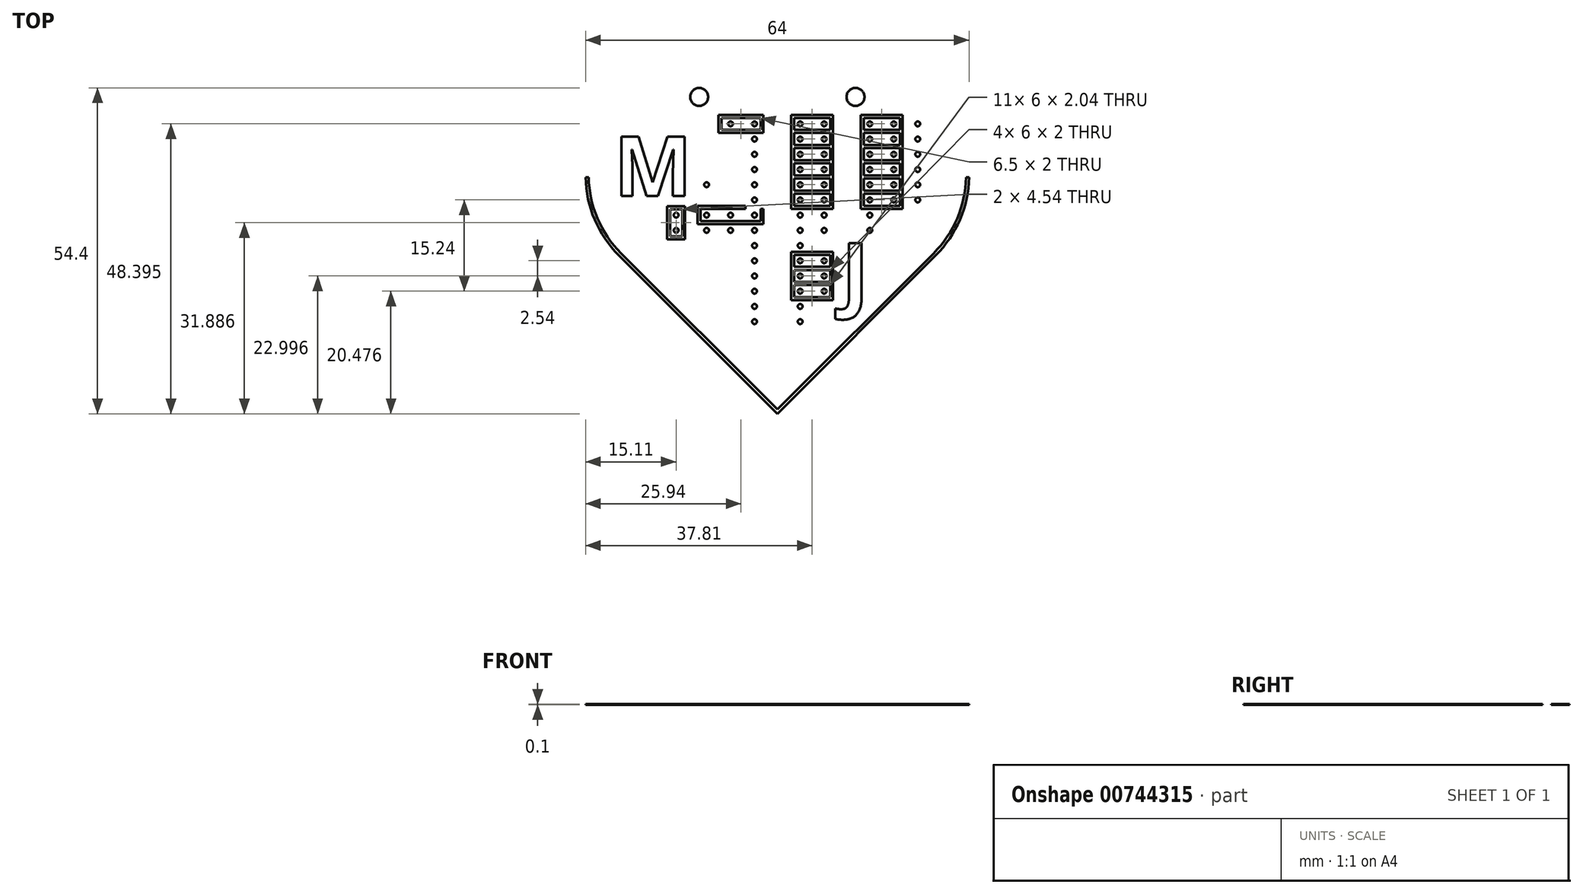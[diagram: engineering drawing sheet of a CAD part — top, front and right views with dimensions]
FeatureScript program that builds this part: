
annotation { "Feature Type Name" : "Feature", "Feature Type Description" : "" }
export const myFeature = defineFeature(function(context is Context, id is Id, definition is map)
    precondition{}
    {
        {
            var Q0;
            Q0=qCreatedBy(makeId("Top.planeOp"),FACE);
            var sketch = newSketch(context, id + "F0", { "sketchPlane" : qUnion([Q0])});
            skLineSegment(sketch, "E0.bottom", {"start": v(0, 0) * mm, "end": v(70, 0) * mm});
            skLineSegment(sketch, "E0.top", {"start": v(0, 100) * mm, "end": v(70, 100) * mm});
            skLineSegment(sketch, "E0.left", {"start": v(0, 0) * mm, "end": v(0, 100) * mm});
            skLineSegment(sketch, "E0.right", {"start": v(70, 0) * mm, "end": v(70, 100) * mm});
            skLineSegment(sketch, "E1", {"start": v(8.9, 50) * mm, "end": v(35, 23.9) * mm});
            skPoint(sketch, "E1.endSnap0", {"position": v(35, 0) * mm});
            skLineSegment(sketch, "E2", {"start": v(35, 23.9) * mm, "end": v(61.1, 50) * mm});
            skPoint(sketch, "E3", {"position": v(0, 50) * mm});
            skArc(sketch, "E4", {"start": v(8.9, 50) * mm, "mid": v(8.9, 76.1) * mm, "end": v(35, 76.1) * mm});
            skArc(sketch, "E5", {"start": v(61.1, 50) * mm, "mid": v(61.1, 76.1) * mm, "end": v(35, 76.1) * mm});
            skLineSegment(sketch, "E6", {"start": v(8.9, 50) * mm, "end": v(35, 76.1) * mm, "construction": true});
            skLineSegment(sketch, "E7", {"start": v(35, 76.1) * mm, "end": v(61.1, 50) * mm, "construction": true});
            skCircle(sketch, "E8", {"center": v(31.2, 38.58) * mm, "radius": 0.4 * mm});
            skCircle(sketch, "E9", {"center": v(31.2, 38.58) * mm, "radius": 1 * mm});
            skCircle(sketch, "E10.1.0.0", {"center": v(31.2, 41.12) * mm, "radius": 1 * mm});
            skCircle(sketch, "E10.1.0.1", {"center": v(31.2, 41.12) * mm, "radius": 0.4 * mm});
            skCircle(sketch, "E10.2.0.0", {"center": v(31.2, 43.66) * mm, "radius": 1 * mm});
            skCircle(sketch, "E10.2.0.1", {"center": v(31.2, 43.66) * mm, "radius": 0.4 * mm});
            skCircle(sketch, "E10.3.0.0", {"center": v(31.2, 46.2) * mm, "radius": 1 * mm});
            skCircle(sketch, "E10.3.0.1", {"center": v(31.2, 46.2) * mm, "radius": 0.4 * mm});
            skCircle(sketch, "E10.4.0.0", {"center": v(31.2, 48.74) * mm, "radius": 1 * mm});
            skCircle(sketch, "E10.4.0.1", {"center": v(31.2, 48.74) * mm, "radius": 0.4 * mm});
            skCircle(sketch, "E10.5.0.0", {"center": v(31.2, 51.28) * mm, "radius": 1 * mm});
            skCircle(sketch, "E10.5.0.1", {"center": v(31.2, 51.28) * mm, "radius": 0.4 * mm});
            skCircle(sketch, "E10.6.0.0", {"center": v(31.2, 53.82) * mm, "radius": 1 * mm});
            skCircle(sketch, "E10.6.0.1", {"center": v(31.2, 53.82) * mm, "radius": 0.4 * mm});
            skCircle(sketch, "E10.7.0.0", {"center": v(31.2, 56.36) * mm, "radius": 1 * mm});
            skCircle(sketch, "E10.7.0.1", {"center": v(31.2, 56.36) * mm, "radius": 0.4 * mm});
            skCircle(sketch, "E10.8.0.0", {"center": v(31.2, 58.9) * mm, "radius": 1 * mm});
            skCircle(sketch, "E10.8.0.1", {"center": v(31.2, 58.9) * mm, "radius": 0.4 * mm});
            skCircle(sketch, "E10.9.0.0", {"center": v(31.2, 61.44) * mm, "radius": 1 * mm});
            skCircle(sketch, "E10.9.0.1", {"center": v(31.2, 61.44) * mm, "radius": 0.4 * mm});
            skCircle(sketch, "E10.10.0.0", {"center": v(31.2, 63.98) * mm, "radius": 1 * mm});
            skCircle(sketch, "E10.10.0.1", {"center": v(31.2, 63.98) * mm, "radius": 0.4 * mm});
            skCircle(sketch, "E10.11.0.0", {"center": v(31.2, 66.52) * mm, "radius": 1 * mm});
            skCircle(sketch, "E10.11.0.1", {"center": v(31.2, 66.52) * mm, "radius": 0.4 * mm});
            skCircle(sketch, "E10.12.0.0", {"center": v(31.2, 69.06) * mm, "radius": 1 * mm});
            skCircle(sketch, "E10.12.0.1", {"center": v(31.2, 69.06) * mm, "radius": 0.4 * mm});
            skCircle(sketch, "E10.13.0.0", {"center": v(31.2, 71.6) * mm, "radius": 1 * mm});
            skCircle(sketch, "E10.13.0.1", {"center": v(31.2, 71.6) * mm, "radius": 0.4 * mm});
            skLineSegment(sketch, "E10.direction1", {"start": v(31.2, 38.58) * mm, "end": v(31.2, 41.12) * mm, "construction": true});
            skCircle(sketch, "E11.1.0.0", {"center": v(38.81, 58.9) * mm, "radius": 1 * mm});
            skCircle(sketch, "E11.1.0.1", {"center": v(38.81, 69.06) * mm, "radius": 1 * mm});
            skCircle(sketch, "E11.1.0.2", {"center": v(38.81, 66.52) * mm, "radius": 1 * mm});
            skCircle(sketch, "E11.1.0.3", {"center": v(38.81, 56.36) * mm, "radius": 1 * mm});
            skCircle(sketch, "E11.1.0.4", {"center": v(38.81, 61.44) * mm, "radius": 1 * mm});
            skCircle(sketch, "E11.1.0.5", {"center": v(38.81, 63.98) * mm, "radius": 1 * mm});
            skCircle(sketch, "E11.1.0.6", {"center": v(38.81, 38.58) * mm, "radius": 1 * mm});
            skCircle(sketch, "E11.1.0.7", {"center": v(38.81, 53.82) * mm, "radius": 1 * mm});
            skCircle(sketch, "E11.1.0.8", {"center": v(38.81, 41.12) * mm, "radius": 1 * mm});
            skCircle(sketch, "E11.1.0.9", {"center": v(38.81, 48.74) * mm, "radius": 1 * mm});
            skCircle(sketch, "E11.1.0.10", {"center": v(38.81, 43.66) * mm, "radius": 1 * mm});
            skCircle(sketch, "E11.1.0.11", {"center": v(38.81, 51.28) * mm, "radius": 1 * mm});
            skCircle(sketch, "E11.1.0.12", {"center": v(38.81, 71.6) * mm, "radius": 1 * mm});
            skCircle(sketch, "E11.1.0.13", {"center": v(38.81, 46.2) * mm, "radius": 1 * mm});
            skLineSegment(sketch, "E11.1.0.14", {"start": v(38.81, 38.58) * mm, "end": v(38.81, 41.12) * mm, "construction": true});
            skCircle(sketch, "E11.1.0.15", {"center": v(38.81, 71.6) * mm, "radius": 0.4 * mm});
            skCircle(sketch, "E11.1.0.16", {"center": v(38.81, 69.06) * mm, "radius": 0.4 * mm});
            skCircle(sketch, "E11.1.0.17", {"center": v(38.81, 66.52) * mm, "radius": 0.4 * mm});
            skCircle(sketch, "E11.1.0.18", {"center": v(38.81, 46.2) * mm, "radius": 0.4 * mm});
            skCircle(sketch, "E11.1.0.19", {"center": v(38.81, 51.28) * mm, "radius": 0.4 * mm});
            skCircle(sketch, "E11.1.0.20", {"center": v(38.81, 48.74) * mm, "radius": 0.4 * mm});
            skCircle(sketch, "E11.1.0.21", {"center": v(38.81, 53.82) * mm, "radius": 0.4 * mm});
            skCircle(sketch, "E11.1.0.22", {"center": v(38.81, 43.66) * mm, "radius": 0.4 * mm});
            skCircle(sketch, "E11.1.0.23", {"center": v(38.81, 56.36) * mm, "radius": 0.4 * mm});
            skCircle(sketch, "E11.1.0.24", {"center": v(38.81, 63.98) * mm, "radius": 0.4 * mm});
            skCircle(sketch, "E11.1.0.25", {"center": v(38.81, 58.9) * mm, "radius": 0.4 * mm});
            skCircle(sketch, "E11.1.0.26", {"center": v(38.81, 61.44) * mm, "radius": 0.4 * mm});
            skCircle(sketch, "E11.1.0.27", {"center": v(38.81, 41.12) * mm, "radius": 0.4 * mm});
            skCircle(sketch, "E11.1.0.28", {"center": v(38.81, 38.58) * mm, "radius": 0.4 * mm});
            skLineSegment(sketch, "E11.direction1", {"start": v(31.2, 38.58) * mm, "end": v(38.81, 38.58) * mm, "construction": true});
            skLineSegment(sketch, "E12.bottom", {"start": v(29.7, 73.1) * mm, "end": v(32.7, 73.1) * mm});
            skLineSegment(sketch, "E12.top", {"start": v(29.7, 37.08) * mm, "end": v(32.7, 37.08) * mm});
            skLineSegment(sketch, "E12.left", {"start": v(29.7, 73.1) * mm, "end": v(29.7, 37.08) * mm});
            skLineSegment(sketch, "E12.right", {"start": v(32.7, 73.1) * mm, "end": v(32.7, 37.08) * mm});
            skLineSegment(sketch, "E13.bottom", {"start": v(37.19, 37.08) * mm, "end": v(40.31, 37.08) * mm});
            skLineSegment(sketch, "E13.top", {"start": v(37.19, 73.1) * mm, "end": v(40.31, 73.1) * mm});
            skLineSegment(sketch, "E13.left", {"start": v(37.19, 37.08) * mm, "end": v(37.19, 73.1) * mm});
            skLineSegment(sketch, "E13.right", {"start": v(40.31, 37.08) * mm, "end": v(40.31, 73.1) * mm});
            skLineSegment(sketch, "E14.bottom", {"start": v(29.7, 54.82) * mm, "end": v(32.7, 54.82) * mm});
            skLineSegment(sketch, "E14.top", {"start": v(29.7, 52.82) * mm, "end": v(32.7, 52.82) * mm});
            skLineSegment(sketch, "E14.left", {"start": v(29.7, 54.82) * mm, "end": v(29.7, 52.82) * mm});
            skLineSegment(sketch, "E14.right", {"start": v(32.7, 54.82) * mm, "end": v(32.7, 52.82) * mm});
            skCircle(sketch, "E15", {"center": v(23.2, 53.82) * mm, "radius": 0.4 * mm});
            skCircle(sketch, "E16", {"center": v(23.2, 56.36) * mm, "radius": 1 * mm});
            skCircle(sketch, "E17", {"center": v(23.2, 56.36) * mm, "radius": 0.4 * mm});
            skLineSegment(sketch, "E18.bottom", {"start": v(24.1, 55.96) * mm, "end": v(30.27, 55.96) * mm});
            skLineSegment(sketch, "E18.top", {"start": v(24.1, 56.76) * mm, "end": v(30.27, 56.76) * mm});
            skLineSegment(sketch, "E18.left", {"start": v(24.1, 55.96) * mm, "end": v(24.1, 56.76) * mm});
            skLineSegment(sketch, "E18.right", {"start": v(30.27, 55.96) * mm, "end": v(30.27, 56.76) * mm});
            skArc(sketch, "E19", {"start": v(24.4, 55.46) * mm, "mid": v(21.7, 56.36) * mm, "end": v(24.4, 57.26) * mm});
            skLineSegment(sketch, "E20", {"start": v(24.4, 57.26) * mm, "end": v(29.7, 57.26) * mm});
            skLineSegment(sketch, "E21", {"start": v(24.4, 55.46) * mm, "end": v(29.7, 55.46) * mm});
            skPoint(sketch, "E21.endSnap0", {"position": v(29.7, 55.09) * mm});
            skLineSegment(sketch, "E22.bottom", {"start": v(37.19, 57.36) * mm, "end": v(40.31, 57.36) * mm});
            skLineSegment(sketch, "E22.top", {"start": v(37.19, 55.36) * mm, "end": v(40.31, 55.36) * mm});
            skLineSegment(sketch, "E22.left", {"start": v(37.19, 57.36) * mm, "end": v(37.19, 55.36) * mm});
            skLineSegment(sketch, "E22.right", {"start": v(40.31, 57.36) * mm, "end": v(40.31, 55.36) * mm});
            skCircle(sketch, "E23", {"center": v(42.81, 58.9) * mm, "radius": 0.4 * mm});
            skCircle(sketch, "E24", {"center": v(42.81, 58.9) * mm, "radius": 1 * mm});
            skLineSegment(sketch, "E25.bottom", {"start": v(41.9, 59.3) * mm, "end": v(39.73, 59.3) * mm});
            skLineSegment(sketch, "E25.top", {"start": v(41.9, 58.5) * mm, "end": v(39.73, 58.5) * mm});
            skLineSegment(sketch, "E25.left", {"start": v(41.9, 59.3) * mm, "end": v(41.9, 58.5) * mm});
            skLineSegment(sketch, "E25.right", {"start": v(39.73, 59.3) * mm, "end": v(39.73, 58.5) * mm});
            skArc(sketch, "E26", {"start": v(41.61, 59.8) * mm, "mid": v(44.31, 58.9) * mm, "end": v(41.61, 58) * mm});
            skLineSegment(sketch, "E27", {"start": v(41.61, 59.8) * mm, "end": v(40.31, 59.8) * mm});
            skLineSegment(sketch, "E28", {"start": v(41.61, 58) * mm, "end": v(40.31, 58) * mm});
            skCircle(sketch, "E29", {"center": v(50.43, 58.9) * mm, "radius": 0.4 * mm});
            skCircle(sketch, "E30", {"center": v(50.43, 58.9) * mm, "radius": 1 * mm});
            skCircle(sketch, "E31", {"center": v(54.43, 58.9) * mm, "radius": 0.4 * mm});
            skCircle(sketch, "E32", {"center": v(54.43, 58.9) * mm, "radius": 1 * mm});
            skCircle(sketch, "E33", {"center": v(58.43, 58.9) * mm, "radius": 0.4 * mm});
            skLineSegment(sketch, "E34.bottom", {"start": v(51.35, 59.3) * mm, "end": v(53.51, 59.3) * mm});
            skLineSegment(sketch, "E34.top", {"start": v(51.35, 58.5) * mm, "end": v(53.51, 58.5) * mm});
            skLineSegment(sketch, "E34.left", {"start": v(51.35, 59.3) * mm, "end": v(51.35, 58.5) * mm});
            skLineSegment(sketch, "E34.right", {"start": v(53.51, 59.3) * mm, "end": v(53.51, 58.5) * mm});
            skArc(sketch, "E35", {"start": v(51.63, 58) * mm, "mid": v(48.93, 58.9) * mm, "end": v(51.63, 59.8) * mm});
            skArc(sketch, "E36", {"start": v(53.23, 58) * mm, "mid": v(55.93, 58.9) * mm, "end": v(53.23, 59.8) * mm});
            skLineSegment(sketch, "E37", {"start": v(51.63, 59.8) * mm, "end": v(53.23, 59.8) * mm});
            skLineSegment(sketch, "E38", {"start": v(51.63, 58) * mm, "end": v(53.23, 58) * mm});
            skCircle(sketch, "E39.1.0.0", {"center": v(54.43, 61.44) * mm, "radius": 1 * mm});
            skArc(sketch, "E39.1.0.1", {"start": v(53.23, 60.54) * mm, "mid": v(55.93, 61.44) * mm, "end": v(53.23, 62.34) * mm});
            skCircle(sketch, "E39.1.0.2", {"center": v(58.43, 61.44) * mm, "radius": 0.4 * mm});
            skLineSegment(sketch, "E39.1.0.3", {"start": v(51.35, 61.04) * mm, "end": v(53.51, 61.04) * mm});
            skLineSegment(sketch, "E39.1.0.4", {"start": v(53.51, 61.84) * mm, "end": v(53.51, 61.04) * mm});
            skLineSegment(sketch, "E39.1.0.5", {"start": v(51.35, 61.84) * mm, "end": v(53.51, 61.84) * mm});
            skLineSegment(sketch, "E39.1.0.6", {"start": v(51.63, 62.34) * mm, "end": v(53.23, 62.34) * mm});
            skLineSegment(sketch, "E39.1.0.7", {"start": v(51.63, 60.54) * mm, "end": v(53.23, 60.54) * mm});
            skArc(sketch, "E39.1.0.8", {"start": v(51.63, 60.54) * mm, "mid": v(48.93, 61.44) * mm, "end": v(51.63, 62.34) * mm});
            skCircle(sketch, "E39.1.0.9", {"center": v(50.43, 61.44) * mm, "radius": 1 * mm});
            skLineSegment(sketch, "E39.1.0.10", {"start": v(51.35, 61.84) * mm, "end": v(51.35, 61.04) * mm});
            skCircle(sketch, "E39.1.0.11", {"center": v(54.43, 61.44) * mm, "radius": 0.4 * mm});
            skCircle(sketch, "E39.1.0.12", {"center": v(50.43, 61.44) * mm, "radius": 0.4 * mm});
            skArc(sketch, "E39.1.0.13", {"start": v(41.61, 62.34) * mm, "mid": v(44.31, 61.44) * mm, "end": v(41.61, 60.54) * mm});
            skCircle(sketch, "E39.1.0.14", {"center": v(42.81, 61.44) * mm, "radius": 1 * mm});
            skCircle(sketch, "E39.1.0.15", {"center": v(42.81, 61.44) * mm, "radius": 0.4 * mm});
            skLineSegment(sketch, "E39.1.0.16", {"start": v(41.9, 61.04) * mm, "end": v(39.73, 61.04) * mm});
            skLineSegment(sketch, "E39.1.0.17", {"start": v(41.9, 61.84) * mm, "end": v(39.73, 61.84) * mm});
            skLineSegment(sketch, "E39.1.0.18", {"start": v(41.61, 62.34) * mm, "end": v(40.31, 62.34) * mm});
            skLineSegment(sketch, "E39.1.0.19", {"start": v(39.73, 61.84) * mm, "end": v(39.73, 61.04) * mm});
            skLineSegment(sketch, "E39.1.0.20", {"start": v(41.9, 61.84) * mm, "end": v(41.9, 61.04) * mm});
            skLineSegment(sketch, "E39.1.0.21", {"start": v(41.61, 60.54) * mm, "end": v(40.31, 60.54) * mm});
            skCircle(sketch, "E39.2.0.0", {"center": v(54.43, 63.98) * mm, "radius": 1 * mm});
            skArc(sketch, "E39.2.0.1", {"start": v(53.23, 63.08) * mm, "mid": v(55.93, 63.98) * mm, "end": v(53.23, 64.88) * mm});
            skCircle(sketch, "E39.2.0.2", {"center": v(58.43, 63.98) * mm, "radius": 0.4 * mm});
            skLineSegment(sketch, "E39.2.0.3", {"start": v(51.35, 63.58) * mm, "end": v(53.51, 63.58) * mm});
            skLineSegment(sketch, "E39.2.0.4", {"start": v(53.51, 64.38) * mm, "end": v(53.51, 63.58) * mm});
            skLineSegment(sketch, "E39.2.0.5", {"start": v(51.35, 64.38) * mm, "end": v(53.51, 64.38) * mm});
            skLineSegment(sketch, "E39.2.0.6", {"start": v(51.63, 64.88) * mm, "end": v(53.23, 64.88) * mm});
            skLineSegment(sketch, "E39.2.0.7", {"start": v(51.63, 63.08) * mm, "end": v(53.23, 63.08) * mm});
            skArc(sketch, "E39.2.0.8", {"start": v(51.63, 63.08) * mm, "mid": v(48.93, 63.98) * mm, "end": v(51.63, 64.88) * mm});
            skCircle(sketch, "E39.2.0.9", {"center": v(50.43, 63.98) * mm, "radius": 1 * mm});
            skLineSegment(sketch, "E39.2.0.10", {"start": v(51.35, 64.38) * mm, "end": v(51.35, 63.58) * mm});
            skCircle(sketch, "E39.2.0.11", {"center": v(54.43, 63.98) * mm, "radius": 0.4 * mm});
            skCircle(sketch, "E39.2.0.12", {"center": v(50.43, 63.98) * mm, "radius": 0.4 * mm});
            skArc(sketch, "E39.2.0.13", {"start": v(41.61, 64.88) * mm, "mid": v(44.31, 63.98) * mm, "end": v(41.61, 63.08) * mm});
            skCircle(sketch, "E39.2.0.14", {"center": v(42.81, 63.98) * mm, "radius": 1 * mm});
            skCircle(sketch, "E39.2.0.15", {"center": v(42.81, 63.98) * mm, "radius": 0.4 * mm});
            skLineSegment(sketch, "E39.2.0.16", {"start": v(41.9, 63.58) * mm, "end": v(39.73, 63.58) * mm});
            skLineSegment(sketch, "E39.2.0.17", {"start": v(41.9, 64.38) * mm, "end": v(39.73, 64.38) * mm});
            skLineSegment(sketch, "E39.2.0.18", {"start": v(41.61, 64.88) * mm, "end": v(40.31, 64.88) * mm});
            skLineSegment(sketch, "E39.2.0.19", {"start": v(39.73, 64.38) * mm, "end": v(39.73, 63.58) * mm});
            skLineSegment(sketch, "E39.2.0.20", {"start": v(41.9, 64.38) * mm, "end": v(41.9, 63.58) * mm});
            skLineSegment(sketch, "E39.2.0.21", {"start": v(41.61, 63.08) * mm, "end": v(40.31, 63.08) * mm});
            skCircle(sketch, "E39.3.0.0", {"center": v(54.43, 66.52) * mm, "radius": 1 * mm});
            skArc(sketch, "E39.3.0.1", {"start": v(53.23, 65.62) * mm, "mid": v(55.93, 66.52) * mm, "end": v(53.23, 67.42) * mm});
            skCircle(sketch, "E39.3.0.2", {"center": v(58.43, 66.52) * mm, "radius": 0.4 * mm});
            skLineSegment(sketch, "E39.3.0.3", {"start": v(51.35, 66.12) * mm, "end": v(53.51, 66.12) * mm});
            skLineSegment(sketch, "E39.3.0.4", {"start": v(53.51, 66.92) * mm, "end": v(53.51, 66.12) * mm});
            skLineSegment(sketch, "E39.3.0.5", {"start": v(51.35, 66.92) * mm, "end": v(53.51, 66.92) * mm});
            skLineSegment(sketch, "E39.3.0.6", {"start": v(51.63, 67.42) * mm, "end": v(53.23, 67.42) * mm});
            skLineSegment(sketch, "E39.3.0.7", {"start": v(51.63, 65.62) * mm, "end": v(53.23, 65.62) * mm});
            skArc(sketch, "E39.3.0.8", {"start": v(51.63, 65.62) * mm, "mid": v(48.93, 66.52) * mm, "end": v(51.63, 67.42) * mm});
            skCircle(sketch, "E39.3.0.9", {"center": v(50.43, 66.52) * mm, "radius": 1 * mm});
            skLineSegment(sketch, "E39.3.0.10", {"start": v(51.35, 66.92) * mm, "end": v(51.35, 66.12) * mm});
            skCircle(sketch, "E39.3.0.11", {"center": v(54.43, 66.52) * mm, "radius": 0.4 * mm});
            skCircle(sketch, "E39.3.0.12", {"center": v(50.43, 66.52) * mm, "radius": 0.4 * mm});
            skArc(sketch, "E39.3.0.13", {"start": v(41.61, 67.42) * mm, "mid": v(44.31, 66.52) * mm, "end": v(41.61, 65.62) * mm});
            skCircle(sketch, "E39.3.0.14", {"center": v(42.81, 66.52) * mm, "radius": 1 * mm});
            skCircle(sketch, "E39.3.0.15", {"center": v(42.81, 66.52) * mm, "radius": 0.4 * mm});
            skLineSegment(sketch, "E39.3.0.16", {"start": v(41.9, 66.12) * mm, "end": v(39.73, 66.12) * mm});
            skLineSegment(sketch, "E39.3.0.17", {"start": v(41.9, 66.92) * mm, "end": v(39.73, 66.92) * mm});
            skLineSegment(sketch, "E39.3.0.18", {"start": v(41.61, 67.42) * mm, "end": v(40.31, 67.42) * mm});
            skLineSegment(sketch, "E39.3.0.19", {"start": v(39.73, 66.92) * mm, "end": v(39.73, 66.12) * mm});
            skLineSegment(sketch, "E39.3.0.20", {"start": v(41.9, 66.92) * mm, "end": v(41.9, 66.12) * mm});
            skLineSegment(sketch, "E39.3.0.21", {"start": v(41.61, 65.62) * mm, "end": v(40.31, 65.62) * mm});
            skCircle(sketch, "E39.4.0.0", {"center": v(54.43, 69.06) * mm, "radius": 1 * mm});
            skArc(sketch, "E39.4.0.1", {"start": v(53.23, 68.16) * mm, "mid": v(55.93, 69.06) * mm, "end": v(53.23, 69.96) * mm});
            skCircle(sketch, "E39.4.0.2", {"center": v(58.43, 69.06) * mm, "radius": 0.4 * mm});
            skLineSegment(sketch, "E39.4.0.3", {"start": v(51.35, 68.66) * mm, "end": v(53.51, 68.66) * mm});
            skLineSegment(sketch, "E39.4.0.4", {"start": v(53.51, 69.46) * mm, "end": v(53.51, 68.66) * mm});
            skLineSegment(sketch, "E39.4.0.5", {"start": v(51.35, 69.46) * mm, "end": v(53.51, 69.46) * mm});
            skLineSegment(sketch, "E39.4.0.6", {"start": v(51.63, 69.96) * mm, "end": v(53.23, 69.96) * mm});
            skLineSegment(sketch, "E39.4.0.7", {"start": v(51.63, 68.16) * mm, "end": v(53.23, 68.16) * mm});
            skArc(sketch, "E39.4.0.8", {"start": v(51.63, 68.16) * mm, "mid": v(48.93, 69.06) * mm, "end": v(51.63, 69.96) * mm});
            skCircle(sketch, "E39.4.0.9", {"center": v(50.43, 69.06) * mm, "radius": 1 * mm});
            skLineSegment(sketch, "E39.4.0.10", {"start": v(51.35, 69.46) * mm, "end": v(51.35, 68.66) * mm});
            skCircle(sketch, "E39.4.0.11", {"center": v(54.43, 69.06) * mm, "radius": 0.4 * mm});
            skCircle(sketch, "E39.4.0.12", {"center": v(50.43, 69.06) * mm, "radius": 0.4 * mm});
            skArc(sketch, "E39.4.0.13", {"start": v(41.61, 69.96) * mm, "mid": v(44.31, 69.06) * mm, "end": v(41.61, 68.16) * mm});
            skCircle(sketch, "E39.4.0.14", {"center": v(42.81, 69.06) * mm, "radius": 1 * mm});
            skCircle(sketch, "E39.4.0.15", {"center": v(42.81, 69.06) * mm, "radius": 0.4 * mm});
            skLineSegment(sketch, "E39.4.0.16", {"start": v(41.9, 68.66) * mm, "end": v(39.73, 68.66) * mm});
            skLineSegment(sketch, "E39.4.0.17", {"start": v(41.9, 69.46) * mm, "end": v(39.73, 69.46) * mm});
            skLineSegment(sketch, "E39.4.0.18", {"start": v(41.61, 69.96) * mm, "end": v(40.31, 69.96) * mm});
            skLineSegment(sketch, "E39.4.0.19", {"start": v(39.73, 69.46) * mm, "end": v(39.73, 68.66) * mm});
            skLineSegment(sketch, "E39.4.0.20", {"start": v(41.9, 69.46) * mm, "end": v(41.9, 68.66) * mm});
            skLineSegment(sketch, "E39.4.0.21", {"start": v(41.61, 68.16) * mm, "end": v(40.31, 68.16) * mm});
            skCircle(sketch, "E39.5.0.0", {"center": v(54.43, 71.6) * mm, "radius": 1 * mm});
            skArc(sketch, "E39.5.0.1", {"start": v(53.23, 70.7) * mm, "mid": v(55.93, 71.6) * mm, "end": v(53.23, 72.5) * mm});
            skCircle(sketch, "E39.5.0.2", {"center": v(58.43, 71.6) * mm, "radius": 0.4 * mm});
            skLineSegment(sketch, "E39.5.0.3", {"start": v(51.35, 71.2) * mm, "end": v(53.51, 71.2) * mm});
            skLineSegment(sketch, "E39.5.0.4", {"start": v(53.51, 72) * mm, "end": v(53.51, 71.2) * mm});
            skLineSegment(sketch, "E39.5.0.5", {"start": v(51.35, 72) * mm, "end": v(53.51, 72) * mm});
            skLineSegment(sketch, "E39.5.0.6", {"start": v(51.63, 72.5) * mm, "end": v(53.23, 72.5) * mm});
            skLineSegment(sketch, "E39.5.0.7", {"start": v(51.63, 70.7) * mm, "end": v(53.23, 70.7) * mm});
            skArc(sketch, "E39.5.0.8", {"start": v(51.63, 70.7) * mm, "mid": v(48.93, 71.6) * mm, "end": v(51.63, 72.5) * mm});
            skCircle(sketch, "E39.5.0.9", {"center": v(50.43, 71.6) * mm, "radius": 1 * mm});
            skLineSegment(sketch, "E39.5.0.10", {"start": v(51.35, 72) * mm, "end": v(51.35, 71.2) * mm});
            skCircle(sketch, "E39.5.0.11", {"center": v(54.43, 71.6) * mm, "radius": 0.4 * mm});
            skCircle(sketch, "E39.5.0.12", {"center": v(50.43, 71.6) * mm, "radius": 0.4 * mm});
            skArc(sketch, "E39.5.0.13", {"start": v(41.61, 72.5) * mm, "mid": v(44.31, 71.6) * mm, "end": v(41.61, 70.7) * mm});
            skCircle(sketch, "E39.5.0.14", {"center": v(42.81, 71.6) * mm, "radius": 1 * mm});
            skCircle(sketch, "E39.5.0.15", {"center": v(42.81, 71.6) * mm, "radius": 0.4 * mm});
            skLineSegment(sketch, "E39.5.0.16", {"start": v(41.9, 71.2) * mm, "end": v(39.73, 71.2) * mm});
            skLineSegment(sketch, "E39.5.0.17", {"start": v(41.9, 72) * mm, "end": v(39.73, 72) * mm});
            skLineSegment(sketch, "E39.5.0.18", {"start": v(41.61, 72.5) * mm, "end": v(40.31, 72.5) * mm});
            skLineSegment(sketch, "E39.5.0.19", {"start": v(39.73, 72) * mm, "end": v(39.73, 71.2) * mm});
            skLineSegment(sketch, "E39.5.0.20", {"start": v(41.9, 72) * mm, "end": v(41.9, 71.2) * mm});
            skLineSegment(sketch, "E39.5.0.21", {"start": v(41.61, 70.7) * mm, "end": v(40.31, 70.7) * mm});
            skLineSegment(sketch, "E39.direction1", {"start": v(39.73, 58.5) * mm, "end": v(39.73, 61.04) * mm, "construction": true});
            skCircle(sketch, "E40", {"center": v(27.2, 56.36) * mm, "radius": 1.5 * mm});
            skCircle(sketch, "E41", {"center": v(27.2, 56.36) * mm, "radius": 0.4 * mm});
            skCircle(sketch, "E42", {"center": v(27.2, 56.36) * mm, "radius": 1 * mm});
            skCircle(sketch, "E43", {"center": v(27.2, 71.6) * mm, "radius": 0.4 * mm});
            skCircle(sketch, "E44", {"center": v(27.2, 71.6) * mm, "radius": 1 * mm});
            skCircle(sketch, "E45", {"center": v(42.81, 43.66) * mm, "radius": 0.4 * mm});
            skCircle(sketch, "E46", {"center": v(42.81, 43.66) * mm, "radius": 1 * mm});
            skLineSegment(sketch, "E47.bottom", {"start": v(41.9, 44.06) * mm, "end": v(39.73, 44.06) * mm});
            skLineSegment(sketch, "E47.top", {"start": v(41.9, 43.26) * mm, "end": v(39.73, 43.26) * mm});
            skLineSegment(sketch, "E47.left", {"start": v(41.9, 44.06) * mm, "end": v(41.9, 43.26) * mm});
            skArc(sketch, "E48", {"start": v(41.61, 44.56) * mm, "mid": v(44.31, 43.66) * mm, "end": v(41.61, 42.76) * mm});
            skLineSegment(sketch, "E49", {"start": v(41.61, 44.56) * mm, "end": v(40.31, 44.56) * mm});
            skLineSegment(sketch, "E50", {"start": v(41.61, 42.76) * mm, "end": v(40.31, 42.76) * mm});
            skArc(sketch, "E51.1.0.0", {"start": v(41.61, 47.1) * mm, "mid": v(44.31, 46.2) * mm, "end": v(41.61, 45.3) * mm});
            skCircle(sketch, "E51.1.0.1", {"center": v(42.81, 46.2) * mm, "radius": 1 * mm});
            skCircle(sketch, "E51.1.0.2", {"center": v(42.81, 46.2) * mm, "radius": 0.4 * mm});
            skLineSegment(sketch, "E51.1.0.3", {"start": v(41.9, 46.6) * mm, "end": v(41.9, 45.8) * mm});
            skLineSegment(sketch, "E51.1.0.4", {"start": v(41.9, 46.6) * mm, "end": v(39.73, 46.6) * mm});
            skLineSegment(sketch, "E51.1.0.5", {"start": v(41.61, 47.1) * mm, "end": v(40.31, 47.1) * mm});
            skLineSegment(sketch, "E51.1.0.6", {"start": v(41.9, 45.8) * mm, "end": v(39.73, 45.8) * mm});
            skLineSegment(sketch, "E51.1.0.7", {"start": v(41.61, 45.3) * mm, "end": v(40.31, 45.3) * mm});
            skArc(sketch, "E51.2.0.0", {"start": v(41.61, 49.64) * mm, "mid": v(44.31, 48.74) * mm, "end": v(41.61, 47.84) * mm});
            skCircle(sketch, "E51.2.0.1", {"center": v(42.81, 48.74) * mm, "radius": 1 * mm});
            skCircle(sketch, "E51.2.0.2", {"center": v(42.81, 48.74) * mm, "radius": 0.4 * mm});
            skLineSegment(sketch, "E51.2.0.3", {"start": v(41.9, 49.14) * mm, "end": v(41.9, 48.34) * mm});
            skLineSegment(sketch, "E51.2.0.4", {"start": v(41.9, 49.14) * mm, "end": v(39.73, 49.14) * mm});
            skLineSegment(sketch, "E51.2.0.5", {"start": v(41.61, 49.64) * mm, "end": v(40.31, 49.64) * mm});
            skLineSegment(sketch, "E51.2.0.6", {"start": v(41.9, 48.34) * mm, "end": v(39.73, 48.34) * mm});
            skLineSegment(sketch, "E51.2.0.7", {"start": v(41.61, 47.84) * mm, "end": v(40.31, 47.84) * mm});
            skLineSegment(sketch, "E51.direction1", {"start": v(39.73, 43.26) * mm, "end": v(39.73, 45.8) * mm, "construction": true});
            skCircle(sketch, "E52", {"center": v(27.2, 53.82) * mm, "radius": 0.4 * mm});
            skLineSegment(sketch, "E53.bottom", {"start": v(28.1, 72) * mm, "end": v(30.27, 72) * mm});
            skLineSegment(sketch, "E53.top", {"start": v(28.1, 71.2) * mm, "end": v(30.27, 71.2) * mm});
            skLineSegment(sketch, "E53.left", {"start": v(28.1, 72) * mm, "end": v(28.1, 71.2) * mm});
            skLineSegment(sketch, "E53.right", {"start": v(30.27, 72) * mm, "end": v(30.27, 71.2) * mm});
            skArc(sketch, "E54", {"start": v(28.4, 70.7) * mm, "mid": v(25.7, 71.6) * mm, "end": v(28.4, 72.5) * mm});
            skLineSegment(sketch, "E55", {"start": v(28.4, 70.7) * mm, "end": v(29.7, 70.7) * mm});
            skLineSegment(sketch, "E56", {"start": v(28.4, 72.5) * mm, "end": v(29.7, 72.5) * mm});
            skCircle(sketch, "E57", {"center": v(42.81, 56.36) * mm, "radius": 0.4 * mm});
            skCircle(sketch, "E58", {"center": v(50.43, 56.36) * mm, "radius": 0.4 * mm});
            skCircle(sketch, "E59", {"center": v(42.81, 53.82) * mm, "radius": 0.4 * mm});
            skCircle(sketch, "E60", {"center": v(50.43, 53.82) * mm, "radius": 0.4 * mm});
            skArc(sketch, "E61.0", {"start": v(8.55, 49.65) * mm, "mid": v(8.38, 76.27) * mm, "end": v(35, 76.8) * mm});
            skLineSegment(sketch, "E61.1", {"start": v(8.55, 49.65) * mm, "end": v(35, 23.2) * mm});
            skLineSegment(sketch, "E61.2", {"start": v(35, 23.2) * mm, "end": v(61.45, 49.65) * mm});
            skArc(sketch, "E61.3", {"start": v(61.45, 49.65) * mm, "mid": v(61.62, 76.27) * mm, "end": v(35, 76.8) * mm});
            skCircle(sketch, "E62", {"center": v(21.95, 76.1) * mm, "radius": 1.5 * mm});
            skCircle(sketch, "E63", {"center": v(48.05, 76.1) * mm, "radius": 1.5 * mm});
            skLineSegment(sketch, "E64", {"start": v(21.95, 76.1) * mm, "end": v(35, 76.1) * mm, "construction": true});
            skLineSegment(sketch, "E65", {"start": v(48.05, 76.1) * mm, "end": v(35, 76.1) * mm, "construction": true});
            skLineSegment(sketch, "E66.bottom", {"start": v(1.44, 63.68) * mm, "end": v(5.44, 63.68) * mm});
            skLineSegment(sketch, "E66.top", {"start": v(1.44, 62.68) * mm, "end": v(5.44, 62.68) * mm});
            skLineSegment(sketch, "E66.left", {"start": v(1.44, 63.68) * mm, "end": v(1.44, 62.68) * mm});
            skLineSegment(sketch, "E66.right", {"start": v(5.44, 63.68) * mm, "end": v(5.44, 62.68) * mm});
            skLineSegment(sketch, "E67.bottom", {"start": v(64.75, 63.68) * mm, "end": v(68.75, 63.68) * mm});
            skLineSegment(sketch, "E67.top", {"start": v(64.75, 62.68) * mm, "end": v(68.75, 62.68) * mm});
            skLineSegment(sketch, "E67.left", {"start": v(64.75, 63.68) * mm, "end": v(64.75, 62.68) * mm});
            skLineSegment(sketch, "E67.right", {"start": v(68.75, 63.68) * mm, "end": v(68.75, 62.68) * mm});
            skCircle(sketch, "E68", {"center": v(23.2, 61.44) * mm, "radius": 0.4 * mm});
            skCircle(sketch, "E69", {"center": v(18.11, 56.36) * mm, "radius": 0.4 * mm});
            skCircle(sketch, "E70", {"center": v(18.11, 53.82) * mm, "radius": 0.4 * mm});
            skCircle(sketch, "E71", {"center": v(18.11, 56.36) * mm, "radius": 1 * mm});
            skCircle(sketch, "E72", {"center": v(18.11, 53.82) * mm, "radius": 1 * mm});
            skCircle(sketch, "E73", {"center": v(18.11, 53.82) * mm, "radius": 1.5 * mm});
            skCircle(sketch, "E74", {"center": v(18.11, 56.36) * mm, "radius": 1.5 * mm});
            skLineSegment(sketch, "E75.bottom", {"start": v(17.71, 55.44) * mm, "end": v(18.51, 55.44) * mm});
            skLineSegment(sketch, "E75.top", {"start": v(17.71, 54.73) * mm, "end": v(18.51, 54.73) * mm});
            skLineSegment(sketch, "E75.left", {"start": v(17.71, 55.44) * mm, "end": v(17.71, 54.73) * mm});
            skLineSegment(sketch, "E75.right", {"start": v(18.51, 55.44) * mm, "end": v(18.51, 54.73) * mm});
            skLineSegment(sketch, "E76", {"start": v(17.41, 55.64) * mm, "end": v(17.41, 54.53) * mm});
            skLineSegment(sketch, "E77", {"start": v(18.81, 55.64) * mm, "end": v(18.81, 54.53) * mm});
            skText(sketch, "E78", { "text": "M", "fontName": "OpenSans-Bold.ttf"});
            skText(sketch, "E79", { "text": "J", "fontName": "OpenSans-Bold.ttf"});
            const initialGuessF0  = {"E78": [0.0077, 0.05953, 1, 0, 0.01], "E79": [0.04569, 0.0418, 1, 0, 0.01]};
            skSetInitialGuess(sketch, initialGuessF0);
            skSolve(sketch);
        }
        {
            var Q0;
            Q0=makeQuery(id+"F0.imprint","IMPRINT",FACE,{"disambiguationData":[TD([[makeQuery(id+"F0.imprint","IMPRINT",EDGE,{"derivedFrom":sQuery(id+"F0.wireOp",EDGE,"E0.bottom")}),1.0]])]});
            var sketch = newSketch(context, id + "F1", { "sketchPlane" : qUnion([Q0])});
            skLineSegment(sketch, "E80.bottom", {"start": v(25.2, 73.1) * mm, "end": v(32.7, 73.1) * mm});
            skLineSegment(sketch, "E80.top", {"start": v(25.2, 70.1) * mm, "end": v(32.7, 70.1) * mm});
            skLineSegment(sketch, "E80.left", {"start": v(25.2, 73.1) * mm, "end": v(25.2, 70.1) * mm});
            skLineSegment(sketch, "E80.right", {"start": v(32.7, 73.1) * mm, "end": v(32.7, 70.1) * mm});
            skLineSegment(sketch, "E81.bottom", {"start": v(25.7, 72.6) * mm, "end": v(32.2, 72.6) * mm});
            skLineSegment(sketch, "E81.top", {"start": v(25.7, 70.6) * mm, "end": v(32.2, 70.6) * mm});
            skLineSegment(sketch, "E81.left", {"start": v(25.7, 72.6) * mm, "end": v(25.7, 70.6) * mm});
            skLineSegment(sketch, "E81.right", {"start": v(32.2, 72.6) * mm, "end": v(32.2, 70.6) * mm});
            skLineSegment(sketch, "E82.bottom", {"start": v(32.7, 70.1) * mm, "end": v(29.7, 70.1) * mm});
            skLineSegment(sketch, "E82.top", {"start": v(32.7, 67.56) * mm, "end": v(29.7, 67.56) * mm});
            skLineSegment(sketch, "E82.left", {"start": v(32.7, 70.1) * mm, "end": v(32.7, 67.56) * mm});
            skLineSegment(sketch, "E82.right", {"start": v(29.7, 70.1) * mm, "end": v(29.7, 67.56) * mm});
            skLineSegment(sketch, "E83.bottom", {"start": v(30.2, 70.1) * mm, "end": v(32.2, 70.1) * mm});
            skLineSegment(sketch, "E83.top", {"start": v(30.2, 68.06) * mm, "end": v(32.2, 68.06) * mm});
            skLineSegment(sketch, "E83.left", {"start": v(30.2, 70.1) * mm, "end": v(30.2, 68.06) * mm});
            skLineSegment(sketch, "E83.right", {"start": v(32.2, 70.1) * mm, "end": v(32.2, 68.06) * mm});
            skLineSegment(sketch, "E84.1.0.0", {"start": v(30.2, 67.56) * mm, "end": v(32.2, 67.56) * mm});
            skLineSegment(sketch, "E84.1.0.1", {"start": v(29.7, 67.56) * mm, "end": v(29.7, 65.02) * mm});
            skLineSegment(sketch, "E84.1.0.2", {"start": v(30.2, 65.52) * mm, "end": v(32.2, 65.52) * mm});
            skLineSegment(sketch, "E84.1.0.3", {"start": v(30.2, 67.56) * mm, "end": v(30.2, 65.52) * mm});
            skLineSegment(sketch, "E84.1.0.4", {"start": v(32.2, 67.56) * mm, "end": v(32.2, 65.52) * mm});
            skLineSegment(sketch, "E84.1.0.5", {"start": v(32.7, 67.56) * mm, "end": v(32.7, 65.02) * mm});
            skLineSegment(sketch, "E84.1.0.6", {"start": v(32.7, 65.02) * mm, "end": v(29.7, 65.02) * mm});
            skLineSegment(sketch, "E84.2.0.0", {"start": v(30.2, 65.02) * mm, "end": v(32.2, 65.02) * mm});
            skLineSegment(sketch, "E84.2.0.1", {"start": v(29.7, 65.02) * mm, "end": v(29.7, 62.48) * mm});
            skLineSegment(sketch, "E84.2.0.2", {"start": v(30.2, 62.98) * mm, "end": v(32.2, 62.98) * mm});
            skLineSegment(sketch, "E84.2.0.3", {"start": v(30.2, 65.02) * mm, "end": v(30.2, 62.98) * mm});
            skLineSegment(sketch, "E84.2.0.4", {"start": v(32.2, 65.02) * mm, "end": v(32.2, 62.98) * mm});
            skLineSegment(sketch, "E84.2.0.5", {"start": v(32.7, 65.02) * mm, "end": v(32.7, 62.48) * mm});
            skLineSegment(sketch, "E84.2.0.6", {"start": v(32.7, 62.48) * mm, "end": v(29.7, 62.48) * mm});
            skLineSegment(sketch, "E84.2.0.7", {"start": v(32.7, 65.02) * mm, "end": v(29.7, 65.02) * mm});
            skLineSegment(sketch, "E84.3.0.0", {"start": v(30.2, 62.48) * mm, "end": v(32.2, 62.48) * mm});
            skLineSegment(sketch, "E84.3.0.1", {"start": v(29.7, 62.48) * mm, "end": v(29.7, 59.94) * mm});
            skLineSegment(sketch, "E84.3.0.2", {"start": v(30.2, 60.44) * mm, "end": v(32.2, 60.44) * mm});
            skLineSegment(sketch, "E84.3.0.3", {"start": v(30.2, 62.48) * mm, "end": v(30.2, 60.44) * mm});
            skLineSegment(sketch, "E84.3.0.4", {"start": v(32.2, 62.48) * mm, "end": v(32.2, 60.44) * mm});
            skLineSegment(sketch, "E84.3.0.5", {"start": v(32.7, 62.48) * mm, "end": v(32.7, 59.94) * mm});
            skLineSegment(sketch, "E84.3.0.6", {"start": v(32.7, 59.94) * mm, "end": v(29.7, 59.94) * mm});
            skLineSegment(sketch, "E84.3.0.7", {"start": v(32.7, 62.48) * mm, "end": v(29.7, 62.48) * mm});
            skLineSegment(sketch, "E84.4.0.0", {"start": v(30.2, 59.94) * mm, "end": v(32.2, 59.94) * mm});
            skLineSegment(sketch, "E84.4.0.1", {"start": v(29.7, 59.94) * mm, "end": v(29.7, 57.4) * mm});
            skLineSegment(sketch, "E84.4.0.2", {"start": v(30.2, 57.9) * mm, "end": v(32.2, 57.9) * mm});
            skLineSegment(sketch, "E84.4.0.3", {"start": v(30.2, 59.94) * mm, "end": v(30.2, 57.9) * mm});
            skLineSegment(sketch, "E84.4.0.4", {"start": v(32.2, 59.94) * mm, "end": v(32.2, 57.9) * mm});
            skLineSegment(sketch, "E84.4.0.5", {"start": v(32.7, 59.94) * mm, "end": v(32.7, 57.4) * mm});
            skLineSegment(sketch, "E84.4.0.6", {"start": v(32.7, 57.4) * mm, "end": v(29.7, 57.4) * mm});
            skLineSegment(sketch, "E84.4.0.7", {"start": v(32.7, 59.94) * mm, "end": v(29.7, 59.94) * mm});
            skLineSegment(sketch, "E84.5.0.0", {"start": v(30.2, 57.4) * mm, "end": v(32.2, 57.4) * mm});
            skLineSegment(sketch, "E84.5.0.1", {"start": v(29.7, 57.4) * mm, "end": v(29.7, 54.86) * mm});
            skLineSegment(sketch, "E84.5.0.2", {"start": v(30.2, 55.36) * mm, "end": v(32.2, 55.36) * mm});
            skLineSegment(sketch, "E84.5.0.3", {"start": v(30.2, 57.4) * mm, "end": v(30.2, 55.36) * mm});
            skLineSegment(sketch, "E84.5.0.4", {"start": v(32.2, 57.4) * mm, "end": v(32.2, 55.36) * mm});
            skLineSegment(sketch, "E84.5.0.5", {"start": v(32.7, 57.4) * mm, "end": v(32.7, 54.86) * mm});
            skLineSegment(sketch, "E84.5.0.6", {"start": v(32.7, 54.86) * mm, "end": v(29.7, 54.86) * mm});
            skLineSegment(sketch, "E84.5.0.7", {"start": v(32.7, 57.4) * mm, "end": v(29.7, 57.4) * mm});
            skLineSegment(sketch, "E84.direction1", {"start": v(29.7, 67.56) * mm, "end": v(29.7, 65.02) * mm, "construction": true});
            skLineSegment(sketch, "E85.bottom", {"start": v(21.7, 57.9) * mm, "end": v(29.7, 57.9) * mm});
            skLineSegment(sketch, "E85.top", {"start": v(21.7, 54.86) * mm, "end": v(29.7, 54.86) * mm});
            skLineSegment(sketch, "E85.left", {"start": v(21.7, 57.9) * mm, "end": v(21.7, 54.86) * mm});
            skLineSegment(sketch, "E85.right", {"start": v(29.7, 57.9) * mm, "end": v(29.7, 54.86) * mm});
            skLineSegment(sketch, "E86.bottom", {"start": v(22.2, 57.4) * mm, "end": v(30.2, 57.4) * mm});
            skLineSegment(sketch, "E86.top", {"start": v(22.2, 55.36) * mm, "end": v(30.2, 55.36) * mm});
            skLineSegment(sketch, "E86.left", {"start": v(22.2, 57.4) * mm, "end": v(22.2, 55.36) * mm});
            skLineSegment(sketch, "E87.bottom", {"start": v(16.61, 57.86) * mm, "end": v(19.61, 57.86) * mm});
            skLineSegment(sketch, "E87.top", {"start": v(16.61, 52.32) * mm, "end": v(19.61, 52.32) * mm});
            skLineSegment(sketch, "E87.left", {"start": v(16.61, 57.86) * mm, "end": v(16.61, 52.32) * mm});
            skLineSegment(sketch, "E87.right", {"start": v(19.61, 57.86) * mm, "end": v(19.61, 52.32) * mm});
            skLineSegment(sketch, "E88.bottom", {"start": v(17.11, 57.36) * mm, "end": v(19.11, 57.36) * mm});
            skLineSegment(sketch, "E88.top", {"start": v(17.11, 52.82) * mm, "end": v(19.11, 52.82) * mm});
            skLineSegment(sketch, "E88.left", {"start": v(17.11, 57.36) * mm, "end": v(17.11, 52.82) * mm});
            skLineSegment(sketch, "E88.right", {"start": v(19.11, 57.36) * mm, "end": v(19.11, 52.82) * mm});
            skLineSegment(sketch, "E89.bottom", {"start": v(37.31, 73.1) * mm, "end": v(44.31, 73.1) * mm});
            skLineSegment(sketch, "E89.top", {"start": v(37.31, 70.1) * mm, "end": v(44.31, 70.1) * mm});
            skLineSegment(sketch, "E89.left", {"start": v(37.31, 73.1) * mm, "end": v(37.31, 70.1) * mm});
            skLineSegment(sketch, "E89.right", {"start": v(44.31, 73.1) * mm, "end": v(44.31, 70.1) * mm});
            skLineSegment(sketch, "E90.bottom", {"start": v(37.81, 72.6) * mm, "end": v(43.81, 72.6) * mm});
            skLineSegment(sketch, "E90.top", {"start": v(37.81, 70.6) * mm, "end": v(43.81, 70.6) * mm});
            skLineSegment(sketch, "E90.left", {"start": v(37.81, 72.6) * mm, "end": v(37.81, 70.6) * mm});
            skLineSegment(sketch, "E90.right", {"start": v(43.81, 72.6) * mm, "end": v(43.81, 70.6) * mm});
            skLineSegment(sketch, "E91.top", {"start": v(37.31, 67.56) * mm, "end": v(44.31, 67.56) * mm});
            skLineSegment(sketch, "E91.left", {"start": v(37.31, 70.1) * mm, "end": v(37.31, 67.56) * mm});
            skLineSegment(sketch, "E91.right", {"start": v(44.31, 70.1) * mm, "end": v(44.31, 67.56) * mm});
            skLineSegment(sketch, "E92.bottom", {"start": v(37.81, 70.1) * mm, "end": v(43.81, 70.1) * mm});
            skLineSegment(sketch, "E92.top", {"start": v(37.81, 68.06) * mm, "end": v(43.81, 68.06) * mm});
            skLineSegment(sketch, "E92.left", {"start": v(37.81, 70.1) * mm, "end": v(37.81, 68.06) * mm});
            skLineSegment(sketch, "E92.right", {"start": v(43.81, 70.1) * mm, "end": v(43.81, 68.06) * mm});
            skLineSegment(sketch, "E93.1.0.0", {"start": v(43.81, 67.56) * mm, "end": v(43.81, 65.52) * mm});
            skLineSegment(sketch, "E93.1.0.1", {"start": v(37.81, 67.56) * mm, "end": v(37.81, 65.52) * mm});
            skLineSegment(sketch, "E93.1.0.2", {"start": v(37.81, 65.52) * mm, "end": v(43.81, 65.52) * mm});
            skLineSegment(sketch, "E93.1.0.3", {"start": v(37.31, 67.56) * mm, "end": v(37.31, 65.02) * mm});
            skLineSegment(sketch, "E93.1.0.4", {"start": v(44.31, 67.56) * mm, "end": v(44.31, 65.02) * mm});
            skLineSegment(sketch, "E93.1.0.5", {"start": v(37.31, 65.02) * mm, "end": v(44.31, 65.02) * mm});
            skLineSegment(sketch, "E93.1.0.6", {"start": v(37.81, 67.56) * mm, "end": v(43.81, 67.56) * mm});
            skLineSegment(sketch, "E93.2.0.0", {"start": v(43.81, 65.02) * mm, "end": v(43.81, 62.98) * mm});
            skLineSegment(sketch, "E93.2.0.1", {"start": v(37.81, 65.02) * mm, "end": v(37.81, 62.98) * mm});
            skLineSegment(sketch, "E93.2.0.2", {"start": v(37.81, 62.98) * mm, "end": v(43.81, 62.98) * mm});
            skLineSegment(sketch, "E93.2.0.3", {"start": v(37.31, 65.02) * mm, "end": v(37.31, 62.48) * mm});
            skLineSegment(sketch, "E93.2.0.4", {"start": v(44.31, 65.02) * mm, "end": v(44.31, 62.48) * mm});
            skLineSegment(sketch, "E93.2.0.5", {"start": v(37.31, 62.48) * mm, "end": v(44.31, 62.48) * mm});
            skLineSegment(sketch, "E93.2.0.6", {"start": v(37.81, 65.02) * mm, "end": v(43.81, 65.02) * mm});
            skLineSegment(sketch, "E93.2.0.7", {"start": v(37.31, 65.02) * mm, "end": v(44.31, 65.02) * mm});
            skLineSegment(sketch, "E93.3.0.0", {"start": v(43.81, 62.48) * mm, "end": v(43.81, 60.44) * mm});
            skLineSegment(sketch, "E93.3.0.1", {"start": v(37.81, 62.48) * mm, "end": v(37.81, 60.44) * mm});
            skLineSegment(sketch, "E93.3.0.2", {"start": v(37.81, 60.44) * mm, "end": v(43.81, 60.44) * mm});
            skLineSegment(sketch, "E93.3.0.3", {"start": v(37.31, 62.48) * mm, "end": v(37.31, 59.94) * mm});
            skLineSegment(sketch, "E93.3.0.4", {"start": v(44.31, 62.48) * mm, "end": v(44.31, 59.94) * mm});
            skLineSegment(sketch, "E93.3.0.5", {"start": v(37.31, 59.94) * mm, "end": v(44.31, 59.94) * mm});
            skLineSegment(sketch, "E93.3.0.6", {"start": v(37.81, 62.48) * mm, "end": v(43.81, 62.48) * mm});
            skLineSegment(sketch, "E93.3.0.7", {"start": v(37.31, 62.48) * mm, "end": v(44.31, 62.48) * mm});
            skLineSegment(sketch, "E93.4.0.0", {"start": v(43.81, 59.94) * mm, "end": v(43.81, 57.9) * mm});
            skLineSegment(sketch, "E93.4.0.1", {"start": v(37.81, 59.94) * mm, "end": v(37.81, 57.9) * mm});
            skLineSegment(sketch, "E93.4.0.2", {"start": v(37.81, 57.9) * mm, "end": v(43.81, 57.9) * mm});
            skLineSegment(sketch, "E93.4.0.3", {"start": v(37.31, 59.94) * mm, "end": v(37.31, 57.4) * mm});
            skLineSegment(sketch, "E93.4.0.4", {"start": v(44.31, 59.94) * mm, "end": v(44.31, 57.4) * mm});
            skLineSegment(sketch, "E93.4.0.5", {"start": v(37.31, 57.4) * mm, "end": v(44.31, 57.4) * mm});
            skLineSegment(sketch, "E93.4.0.6", {"start": v(37.81, 59.94) * mm, "end": v(43.81, 59.94) * mm});
            skLineSegment(sketch, "E93.4.0.7", {"start": v(37.31, 59.94) * mm, "end": v(44.31, 59.94) * mm});
            skLineSegment(sketch, "E93.direction1", {"start": v(37.31, 67.56) * mm, "end": v(37.31, 65.02) * mm, "construction": true});
            skLineSegment(sketch, "E94.bottom", {"start": v(48.93, 73.1) * mm, "end": v(55.93, 73.1) * mm});
            skLineSegment(sketch, "E94.top", {"start": v(48.93, 70.1) * mm, "end": v(55.93, 70.1) * mm});
            skLineSegment(sketch, "E94.left", {"start": v(48.93, 73.1) * mm, "end": v(48.93, 70.1) * mm});
            skLineSegment(sketch, "E94.right", {"start": v(55.93, 73.1) * mm, "end": v(55.93, 70.1) * mm});
            skLineSegment(sketch, "E95.bottom", {"start": v(49.43, 72.6) * mm, "end": v(55.43, 72.6) * mm});
            skLineSegment(sketch, "E95.top", {"start": v(49.43, 70.6) * mm, "end": v(55.43, 70.6) * mm});
            skLineSegment(sketch, "E95.left", {"start": v(49.43, 72.6) * mm, "end": v(49.43, 70.6) * mm});
            skLineSegment(sketch, "E95.right", {"start": v(55.43, 72.6) * mm, "end": v(55.43, 70.6) * mm});
            skLineSegment(sketch, "E96.top", {"start": v(48.93, 67.56) * mm, "end": v(55.93, 67.56) * mm});
            skLineSegment(sketch, "E96.left", {"start": v(48.93, 70.1) * mm, "end": v(48.93, 67.56) * mm});
            skLineSegment(sketch, "E96.right", {"start": v(55.93, 70.1) * mm, "end": v(55.93, 67.56) * mm});
            skLineSegment(sketch, "E97.bottom", {"start": v(49.43, 70.1) * mm, "end": v(55.43, 70.1) * mm});
            skLineSegment(sketch, "E97.top", {"start": v(49.43, 68.06) * mm, "end": v(55.43, 68.06) * mm});
            skLineSegment(sketch, "E97.left", {"start": v(49.43, 70.1) * mm, "end": v(49.43, 68.06) * mm});
            skLineSegment(sketch, "E97.right", {"start": v(55.43, 70.1) * mm, "end": v(55.43, 68.06) * mm});
            skLineSegment(sketch, "E98.1.0.0", {"start": v(55.43, 67.56) * mm, "end": v(55.43, 65.52) * mm});
            skLineSegment(sketch, "E98.1.0.1", {"start": v(49.43, 67.56) * mm, "end": v(49.43, 65.52) * mm});
            skLineSegment(sketch, "E98.1.0.2", {"start": v(49.43, 65.52) * mm, "end": v(55.43, 65.52) * mm});
            skLineSegment(sketch, "E98.1.0.3", {"start": v(48.93, 67.56) * mm, "end": v(48.93, 65.02) * mm});
            skLineSegment(sketch, "E98.1.0.4", {"start": v(55.93, 67.56) * mm, "end": v(55.93, 65.02) * mm});
            skLineSegment(sketch, "E98.1.0.5", {"start": v(48.93, 65.02) * mm, "end": v(55.93, 65.02) * mm});
            skLineSegment(sketch, "E98.1.0.6", {"start": v(49.43, 67.56) * mm, "end": v(55.43, 67.56) * mm});
            skLineSegment(sketch, "E98.2.0.0", {"start": v(55.43, 65.02) * mm, "end": v(55.43, 62.98) * mm});
            skLineSegment(sketch, "E98.2.0.1", {"start": v(49.43, 65.02) * mm, "end": v(49.43, 62.98) * mm});
            skLineSegment(sketch, "E98.2.0.2", {"start": v(49.43, 62.98) * mm, "end": v(55.43, 62.98) * mm});
            skLineSegment(sketch, "E98.2.0.3", {"start": v(48.93, 65.02) * mm, "end": v(48.93, 62.48) * mm});
            skLineSegment(sketch, "E98.2.0.4", {"start": v(55.93, 65.02) * mm, "end": v(55.93, 62.48) * mm});
            skLineSegment(sketch, "E98.2.0.5", {"start": v(48.93, 62.48) * mm, "end": v(55.93, 62.48) * mm});
            skLineSegment(sketch, "E98.2.0.6", {"start": v(49.43, 65.02) * mm, "end": v(55.43, 65.02) * mm});
            skLineSegment(sketch, "E98.2.0.7", {"start": v(48.93, 65.02) * mm, "end": v(55.93, 65.02) * mm});
            skLineSegment(sketch, "E98.3.0.0", {"start": v(55.43, 62.48) * mm, "end": v(55.43, 60.44) * mm});
            skLineSegment(sketch, "E98.3.0.1", {"start": v(49.43, 62.48) * mm, "end": v(49.43, 60.44) * mm});
            skLineSegment(sketch, "E98.3.0.2", {"start": v(49.43, 60.44) * mm, "end": v(55.43, 60.44) * mm});
            skLineSegment(sketch, "E98.3.0.3", {"start": v(48.93, 62.48) * mm, "end": v(48.93, 59.94) * mm});
            skLineSegment(sketch, "E98.3.0.4", {"start": v(55.93, 62.48) * mm, "end": v(55.93, 59.94) * mm});
            skLineSegment(sketch, "E98.3.0.5", {"start": v(48.93, 59.94) * mm, "end": v(55.93, 59.94) * mm});
            skLineSegment(sketch, "E98.3.0.6", {"start": v(49.43, 62.48) * mm, "end": v(55.43, 62.48) * mm});
            skLineSegment(sketch, "E98.3.0.7", {"start": v(48.93, 62.48) * mm, "end": v(55.93, 62.48) * mm});
            skLineSegment(sketch, "E98.4.0.0", {"start": v(55.43, 59.94) * mm, "end": v(55.43, 57.9) * mm});
            skLineSegment(sketch, "E98.4.0.1", {"start": v(49.43, 59.94) * mm, "end": v(49.43, 57.9) * mm});
            skLineSegment(sketch, "E98.4.0.2", {"start": v(49.43, 57.9) * mm, "end": v(55.43, 57.9) * mm});
            skLineSegment(sketch, "E98.4.0.3", {"start": v(48.93, 59.94) * mm, "end": v(48.93, 57.4) * mm});
            skLineSegment(sketch, "E98.4.0.4", {"start": v(55.93, 59.94) * mm, "end": v(55.93, 57.4) * mm});
            skLineSegment(sketch, "E98.4.0.5", {"start": v(48.93, 57.4) * mm, "end": v(55.93, 57.4) * mm});
            skLineSegment(sketch, "E98.4.0.6", {"start": v(49.43, 59.94) * mm, "end": v(55.43, 59.94) * mm});
            skLineSegment(sketch, "E98.4.0.7", {"start": v(48.93, 59.94) * mm, "end": v(55.93, 59.94) * mm});
            skLineSegment(sketch, "E98.direction1", {"start": v(48.93, 67.56) * mm, "end": v(48.93, 65.02) * mm, "construction": true});
            skLineSegment(sketch, "E99.bottom", {"start": v(37.31, 50.24) * mm, "end": v(44.31, 50.24) * mm});
            skLineSegment(sketch, "E99.top", {"start": v(37.31, 47.2) * mm, "end": v(44.31, 47.2) * mm});
            skLineSegment(sketch, "E99.left", {"start": v(37.31, 50.24) * mm, "end": v(37.31, 47.2) * mm});
            skLineSegment(sketch, "E99.right", {"start": v(44.31, 50.24) * mm, "end": v(44.31, 47.2) * mm});
            skLineSegment(sketch, "E100.bottom", {"start": v(37.81, 49.74) * mm, "end": v(43.81, 49.74) * mm});
            skLineSegment(sketch, "E100.top", {"start": v(37.81, 47.74) * mm, "end": v(43.81, 47.74) * mm});
            skLineSegment(sketch, "E100.left", {"start": v(37.81, 49.74) * mm, "end": v(37.81, 47.74) * mm});
            skLineSegment(sketch, "E100.right", {"start": v(43.81, 49.74) * mm, "end": v(43.81, 47.74) * mm});
            skLineSegment(sketch, "E101.top", {"start": v(37.31, 44.7) * mm, "end": v(44.31, 44.7) * mm});
            skLineSegment(sketch, "E101.left", {"start": v(37.31, 47.2) * mm, "end": v(37.31, 44.7) * mm});
            skLineSegment(sketch, "E101.right", {"start": v(44.31, 47.2) * mm, "end": v(44.31, 44.7) * mm});
            skLineSegment(sketch, "E102.bottom", {"start": v(37.81, 47.2) * mm, "end": v(43.81, 47.2) * mm});
            skLineSegment(sketch, "E102.top", {"start": v(37.81, 45.2) * mm, "end": v(43.81, 45.2) * mm});
            skLineSegment(sketch, "E102.left", {"start": v(37.81, 47.2) * mm, "end": v(37.81, 45.2) * mm});
            skLineSegment(sketch, "E102.right", {"start": v(43.81, 47.2) * mm, "end": v(43.81, 45.2) * mm});
            skLineSegment(sketch, "E103.1.0.0", {"start": v(43.81, 44.7) * mm, "end": v(43.81, 42.66) * mm});
            skLineSegment(sketch, "E103.1.0.1", {"start": v(37.81, 44.7) * mm, "end": v(37.81, 42.66) * mm});
            skLineSegment(sketch, "E103.1.0.2", {"start": v(37.81, 42.66) * mm, "end": v(43.81, 42.66) * mm});
            skLineSegment(sketch, "E103.1.0.3", {"start": v(37.31, 44.7) * mm, "end": v(37.31, 42.16) * mm});
            skLineSegment(sketch, "E103.1.0.4", {"start": v(44.31, 44.7) * mm, "end": v(44.31, 42.16) * mm});
            skLineSegment(sketch, "E103.1.0.5", {"start": v(37.31, 42.16) * mm, "end": v(44.31, 42.16) * mm});
            skLineSegment(sketch, "E103.1.0.6", {"start": v(37.81, 44.7) * mm, "end": v(43.81, 44.7) * mm});
            skLineSegment(sketch, "E103.direction1", {"start": v(37.31, 44.7) * mm, "end": v(37.31, 42.16) * mm, "construction": true});
            skLineSegment(sketch, "E104", {"start": v(29.7, 57.9) * mm, "end": v(32.7, 57.9) * mm});
            skSolve(sketch);
        }
        {
            var Q0;
            Q0=makeQuery(id+"F1.imprint","IMPRINT",FACE,{"disambiguationData":[TD([[makeQuery(id+"F1.imprint","IMPRINT",EDGE,{"derivedFrom":sQuery(id+"F1.wireOp",EDGE,"E80.bottom")}),-1.0]])]});
            var Q1;
            {var subQ1=sQuery(id+"F1.wireOp",EDGE,"E85.bottom");Q1=makeQuery(id+"F1.imprint","IMPRINT",FACE,{"disambiguationData":[TD([[makeQuery(id+"F1.imprint","IMPRINT",EDGE,{"derivedFrom":subQ1}),-1.0]])]});}
            var Q2;
            {var subQ3=sQuery(id+"F1.wireOp",EDGE,"E84.5.0.2");Q2=makeQuery(id+"F1.imprint","IMPRINT",FACE,{"disambiguationData":[TD([[makeQuery(id+"F1.imprint","IMPRINT",EDGE,{"derivedFrom":subQ3}),-1.0]])]});}
            var Q3;
            Q3=makeQuery(id+"F1.imprint","IMPRINT",FACE,{"disambiguationData":[TD([[makeQuery(id+"F1.imprint","IMPRINT",EDGE,{"derivedFrom":sQuery(id+"F1.wireOp",EDGE,"E87.bottom")}),-1.0]])]});
            var Q4;
            {var subQ2=sQuery(id+"F1.wireOp",EDGE,"E93.4.0.0");Q4=makeQuery(id+"F1.imprint","IMPRINT",FACE,{"disambiguationData":[TD([[makeQuery(id+"F1.imprint","IMPRINT",EDGE,{"derivedFrom":subQ2}),1.0]])]});}
            var Q5;
            {var subQ4=sQuery(id+"F1.wireOp",EDGE,"E93.3.0.0");Q5=makeQuery(id+"F1.imprint","IMPRINT",FACE,{"disambiguationData":[TD([[makeQuery(id+"F1.imprint","IMPRINT",EDGE,{"derivedFrom":subQ4}),1.0]])]});}
            var Q6;
            {var subQ5=sQuery(id+"F1.wireOp",EDGE,"E93.2.0.0");Q6=makeQuery(id+"F1.imprint","IMPRINT",FACE,{"disambiguationData":[TD([[makeQuery(id+"F1.imprint","IMPRINT",EDGE,{"derivedFrom":subQ5}),1.0]])]});}
            var Q7;
            {var subQ5=sQuery(id+"F1.wireOp",EDGE,"E93.1.0.0");Q7=makeQuery(id+"F1.imprint","IMPRINT",FACE,{"disambiguationData":[TD([[makeQuery(id+"F1.imprint","IMPRINT",EDGE,{"derivedFrom":subQ5}),1.0]])]});}
            var Q8;
            {var subQ4=sQuery(id+"F1.wireOp",EDGE,"E91.left");Q8=makeQuery(id+"F1.imprint","IMPRINT",FACE,{"disambiguationData":[TD([[makeQuery(id+"F1.imprint","IMPRINT",EDGE,{"derivedFrom":subQ4}),1.0]])]});}
            var Q9;
            Q9=makeQuery(id+"F1.imprint","IMPRINT",FACE,{"disambiguationData":[TD([[makeQuery(id+"F1.imprint","IMPRINT",EDGE,{"derivedFrom":sQuery(id+"F1.wireOp",EDGE,"E89.bottom")}),-1.0]])]});
            var Q10;
            Q10=makeQuery(id+"F1.imprint","IMPRINT",FACE,{"disambiguationData":[TD([[makeQuery(id+"F1.imprint","IMPRINT",EDGE,{"derivedFrom":sQuery(id+"F1.wireOp",EDGE,"E94.bottom")}),-1.0]])]});
            var Q11;
            {var subQ4=sQuery(id+"F1.wireOp",EDGE,"E96.left");Q11=makeQuery(id+"F1.imprint","IMPRINT",FACE,{"disambiguationData":[TD([[makeQuery(id+"F1.imprint","IMPRINT",EDGE,{"derivedFrom":subQ4}),1.0]])]});}
            var Q12;
            {var subQ5=sQuery(id+"F1.wireOp",EDGE,"E98.1.0.0");Q12=makeQuery(id+"F1.imprint","IMPRINT",FACE,{"disambiguationData":[TD([[makeQuery(id+"F1.imprint","IMPRINT",EDGE,{"derivedFrom":subQ5}),1.0]])]});}
            var Q13;
            {var subQ5=sQuery(id+"F1.wireOp",EDGE,"E98.2.0.0");Q13=makeQuery(id+"F1.imprint","IMPRINT",FACE,{"disambiguationData":[TD([[makeQuery(id+"F1.imprint","IMPRINT",EDGE,{"derivedFrom":subQ5}),1.0]])]});}
            var Q14;
            {var subQ4=sQuery(id+"F1.wireOp",EDGE,"E98.3.0.0");Q14=makeQuery(id+"F1.imprint","IMPRINT",FACE,{"disambiguationData":[TD([[makeQuery(id+"F1.imprint","IMPRINT",EDGE,{"derivedFrom":subQ4}),1.0]])]});}
            var Q15;
            {var subQ2=sQuery(id+"F1.wireOp",EDGE,"E98.4.0.0");Q15=makeQuery(id+"F1.imprint","IMPRINT",FACE,{"disambiguationData":[TD([[makeQuery(id+"F1.imprint","IMPRINT",EDGE,{"derivedFrom":subQ2}),1.0]])]});}
            var Q16;
            Q16=makeQuery(id+"F1.imprint","IMPRINT",FACE,{"disambiguationData":[TD([[makeQuery(id+"F1.imprint","IMPRINT",EDGE,{"derivedFrom":sQuery(id+"F1.wireOp",EDGE,"E99.bottom")}),-1.0]])]});
            var Q17;
            {var subQ2=sQuery(id+"F1.wireOp",EDGE,"E101.left");Q17=makeQuery(id+"F1.imprint","IMPRINT",FACE,{"disambiguationData":[TD([[makeQuery(id+"F1.imprint","IMPRINT",EDGE,{"derivedFrom":subQ2}),1.0]])]});}
            var Q18;
            {var subQ2=sQuery(id+"F1.wireOp",EDGE,"E103.1.0.0");Q18=makeQuery(id+"F1.imprint","IMPRINT",FACE,{"disambiguationData":[TD([[makeQuery(id+"F1.imprint","IMPRINT",EDGE,{"derivedFrom":subQ2}),1.0]])]});}
            var Q19;
            {var subQ4=sQuery(id+"F1.wireOp",EDGE,"E104");var subQ12=makeQuery(id+"F1.imprint","INTERSECT",VERTEX,{"derivedFrom":[sQuery(id+"F1.wireOp",EDGE,"E84.4.0.3"),subQ4]});Q19=makeQuery(id+"F1.imprint","IMPRINT",FACE,{"disambiguationData":[TD([[makeQuery(id+"F1.imprint","IMPRINT",EDGE,{"disambiguationData":[TD([[subQ12,-1.0]])],"derivedFrom":subQ4}),-1.0]])]});}
            extrude(context, id + "F2", {"entities" : qUnion([Q0, Q1, Q2, Q3, Q4, Q5, Q6, Q7, Q8, Q9, Q10, Q11, Q12, Q13, Q14, Q15, Q16, Q17, Q18, Q19]), "depth" : .1 * mm, "offsetDistance" : 25 * mm});
        }
        {
            var Q0;
            Q0=makeQuery(id+"F0.imprint","IMPRINT",FACE,{"disambiguationData":[TD([[makeQuery(id+"F0.imprint","IMPRINT",EDGE,{"derivedFrom":sQuery(id+"F0.wireOp",EDGE,"E62")}),1.0]])]});
            var Q1;
            Q1=makeQuery(id+"F0.imprint","IMPRINT",FACE,{"disambiguationData":[TD([[makeQuery(id+"F0.imprint","IMPRINT",EDGE,{"derivedFrom":sQuery(id+"F0.wireOp",EDGE,"E63")}),1.0]])]});
            var Q2;
            Q2=makeQuery(id+"F0.imprint","IMPRINT",FACE,{"disambiguationData":[TD([[makeQuery(id+"F0.imprint","IMPRINT",EDGE,{"derivedFrom":sQuery(id+"F0.wireOp",EDGE,"E1")}),-1.0]])]});
            var Q3;
            {var subQ7=sQuery(id+"F0.wireOp",EDGE,"E5");var subQ8=sQuery(id+"F0.wireOp",EDGE,"E4");var subQ9=makeQuery(id+"F0.imprint","INTERSECT",VERTEX,{"derivedFrom":[subQ8,subQ7]});Q3=makeQuery(id+"F0.imprint","IMPRINT",FACE,{"disambiguationData":[TD([[makeQuery(id+"F0.imprint","IMPRINT",EDGE,{"disambiguationData":[TD([[subQ9,1.0]])],"derivedFrom":subQ8}),1.0]])]});}
            extrude(context, id + "F3", {"entities" : qUnion([Q0, Q1, Q2, Q3]), "depth" : .1 * mm, "offsetDistance" : 25 * mm});
        }
        {
            var Q0;
            Q0=makeQuery(id+"F0.imprint","IMPRINT",FACE,{"disambiguationData":[TD([[makeQuery(id+"F0.imprint","IMPRINT",EDGE,{"derivedFrom":sQuery(id+"F0.wireOp",EDGE,"E43")}),1.0]])]});
            var Q1;
            Q1=makeQuery(id+"F0.imprint","IMPRINT",FACE,{"disambiguationData":[TD([[makeQuery(id+"F0.imprint","IMPRINT",EDGE,{"derivedFrom":sQuery(id+"F0.wireOp",EDGE,"E10.13.0.1")}),1.0]])]});
            var Q2;
            Q2=makeQuery(id+"F0.imprint","IMPRINT",FACE,{"disambiguationData":[TD([[makeQuery(id+"F0.imprint","IMPRINT",EDGE,{"derivedFrom":sQuery(id+"F0.wireOp",EDGE,"E10.12.0.1")}),1.0]])]});
            var Q3;
            Q3=makeQuery(id+"F0.imprint","IMPRINT",FACE,{"disambiguationData":[TD([[makeQuery(id+"F0.imprint","IMPRINT",EDGE,{"derivedFrom":sQuery(id+"F0.wireOp",EDGE,"E10.11.0.1")}),1.0]])]});
            var Q4;
            Q4=makeQuery(id+"F0.imprint","IMPRINT",FACE,{"disambiguationData":[TD([[makeQuery(id+"F0.imprint","IMPRINT",EDGE,{"derivedFrom":sQuery(id+"F0.wireOp",EDGE,"E10.10.0.1")}),1.0]])]});
            var Q5;
            Q5=makeQuery(id+"F0.imprint","IMPRINT",FACE,{"disambiguationData":[TD([[makeQuery(id+"F0.imprint","IMPRINT",EDGE,{"derivedFrom":sQuery(id+"F0.wireOp",EDGE,"E10.9.0.1")}),1.0]])]});
            var Q6;
            Q6=makeQuery(id+"F0.imprint","IMPRINT",FACE,{"disambiguationData":[TD([[makeQuery(id+"F0.imprint","IMPRINT",EDGE,{"derivedFrom":sQuery(id+"F0.wireOp",EDGE,"E10.8.0.1")}),1.0]])]});
            var Q7;
            Q7=makeQuery(id+"F0.imprint","IMPRINT",FACE,{"disambiguationData":[TD([[makeQuery(id+"F0.imprint","IMPRINT",EDGE,{"derivedFrom":sQuery(id+"F0.wireOp",EDGE,"E10.7.0.1")}),1.0]])]});
            var Q8;
            {var subQ0=sQuery(id+"F0.wireOp",EDGE,"E41");var subQ1=makeQuery(id+"F0.imprint","INTERSECT",VERTEX,{"derivedFrom":[sQuery(id+"F0.wireOp",EDGE,"E18.bottom"),subQ0]});Q8=makeQuery(id+"F0.imprint","IMPRINT",FACE,{"disambiguationData":[TD([[makeQuery(id+"F0.imprint","IMPRINT",EDGE,{"disambiguationData":[TD([[subQ1,1.0]])],"derivedFrom":subQ0}),1.0]])]});}
            var Q9;
            Q9=makeQuery(id+"F0.imprint","IMPRINT",FACE,{"disambiguationData":[TD([[makeQuery(id+"F0.imprint","IMPRINT",EDGE,{"derivedFrom":sQuery(id+"F0.wireOp",EDGE,"E17")}),1.0]])]});
            var Q10;
            Q10=makeQuery(id+"F0.imprint","IMPRINT",FACE,{"disambiguationData":[TD([[makeQuery(id+"F0.imprint","IMPRINT",EDGE,{"derivedFrom":sQuery(id+"F0.wireOp",EDGE,"E8")}),1.0]])]});
            var Q11;
            Q11=makeQuery(id+"F0.imprint","IMPRINT",FACE,{"disambiguationData":[TD([[makeQuery(id+"F0.imprint","IMPRINT",EDGE,{"derivedFrom":sQuery(id+"F0.wireOp",EDGE,"E10.1.0.1")}),1.0]])]});
            var Q12;
            Q12=makeQuery(id+"F0.imprint","IMPRINT",FACE,{"disambiguationData":[TD([[makeQuery(id+"F0.imprint","IMPRINT",EDGE,{"derivedFrom":sQuery(id+"F0.wireOp",EDGE,"E10.2.0.1")}),1.0]])]});
            var Q13;
            Q13=makeQuery(id+"F0.imprint","IMPRINT",FACE,{"disambiguationData":[TD([[makeQuery(id+"F0.imprint","IMPRINT",EDGE,{"derivedFrom":sQuery(id+"F0.wireOp",EDGE,"E10.3.0.1")}),1.0]])]});
            var Q14;
            Q14=makeQuery(id+"F0.imprint","IMPRINT",FACE,{"disambiguationData":[TD([[makeQuery(id+"F0.imprint","IMPRINT",EDGE,{"derivedFrom":sQuery(id+"F0.wireOp",EDGE,"E10.4.0.1")}),1.0]])]});
            var Q15;
            Q15=makeQuery(id+"F0.imprint","IMPRINT",FACE,{"disambiguationData":[TD([[makeQuery(id+"F0.imprint","IMPRINT",EDGE,{"derivedFrom":sQuery(id+"F0.wireOp",EDGE,"E10.5.0.1")}),1.0]])]});
            var Q16;
            Q16=makeQuery(id+"F0.imprint","IMPRINT",FACE,{"disambiguationData":[TD([[makeQuery(id+"F0.imprint","IMPRINT",EDGE,{"derivedFrom":sQuery(id+"F0.wireOp",EDGE,"E10.6.0.1")}),1.0]])]});
            var Q17;
            Q17=makeQuery(id+"F0.imprint","IMPRINT",FACE,{"disambiguationData":[TD([[makeQuery(id+"F0.imprint","IMPRINT",EDGE,{"derivedFrom":sQuery(id+"F0.wireOp",EDGE,"E11.1.0.28")}),1.0]])]});
            var Q18;
            Q18=makeQuery(id+"F0.imprint","IMPRINT",FACE,{"disambiguationData":[TD([[makeQuery(id+"F0.imprint","IMPRINT",EDGE,{"derivedFrom":sQuery(id+"F0.wireOp",EDGE,"E11.1.0.27")}),1.0]])]});
            var Q19;
            Q19=makeQuery(id+"F0.imprint","IMPRINT",FACE,{"disambiguationData":[TD([[makeQuery(id+"F0.imprint","IMPRINT",EDGE,{"derivedFrom":sQuery(id+"F0.wireOp",EDGE,"E11.1.0.22")}),1.0]])]});
            var Q20;
            Q20=makeQuery(id+"F0.imprint","IMPRINT",FACE,{"disambiguationData":[TD([[makeQuery(id+"F0.imprint","IMPRINT",EDGE,{"derivedFrom":sQuery(id+"F0.wireOp",EDGE,"E45")}),1.0]])]});
            var Q21;
            Q21=makeQuery(id+"F0.imprint","IMPRINT",FACE,{"disambiguationData":[TD([[makeQuery(id+"F0.imprint","IMPRINT",EDGE,{"derivedFrom":sQuery(id+"F0.wireOp",EDGE,"E51.1.0.2")}),1.0]])]});
            var Q22;
            Q22=makeQuery(id+"F0.imprint","IMPRINT",FACE,{"disambiguationData":[TD([[makeQuery(id+"F0.imprint","IMPRINT",EDGE,{"derivedFrom":sQuery(id+"F0.wireOp",EDGE,"E51.2.0.2")}),1.0]])]});
            var Q23;
            Q23=makeQuery(id+"F0.imprint","IMPRINT",FACE,{"disambiguationData":[TD([[makeQuery(id+"F0.imprint","IMPRINT",EDGE,{"derivedFrom":sQuery(id+"F0.wireOp",EDGE,"E11.1.0.20")}),1.0]])]});
            var Q24;
            Q24=makeQuery(id+"F0.imprint","IMPRINT",FACE,{"disambiguationData":[TD([[makeQuery(id+"F0.imprint","IMPRINT",EDGE,{"derivedFrom":sQuery(id+"F0.wireOp",EDGE,"E11.1.0.19")}),1.0]])]});
            var Q25;
            Q25=makeQuery(id+"F0.imprint","IMPRINT",FACE,{"disambiguationData":[TD([[makeQuery(id+"F0.imprint","IMPRINT",EDGE,{"derivedFrom":sQuery(id+"F0.wireOp",EDGE,"E11.1.0.21")}),1.0]])]});
            var Q26;
            Q26=makeQuery(id+"F0.imprint","IMPRINT",FACE,{"disambiguationData":[TD([[makeQuery(id+"F0.imprint","IMPRINT",EDGE,{"derivedFrom":sQuery(id+"F0.wireOp",EDGE,"E11.1.0.23")}),1.0]])]});
            var Q27;
            Q27=makeQuery(id+"F0.imprint","IMPRINT",FACE,{"disambiguationData":[TD([[makeQuery(id+"F0.imprint","IMPRINT",EDGE,{"derivedFrom":sQuery(id+"F0.wireOp",EDGE,"E11.1.0.25")}),1.0]])]});
            var Q28;
            Q28=makeQuery(id+"F0.imprint","IMPRINT",FACE,{"disambiguationData":[TD([[makeQuery(id+"F0.imprint","IMPRINT",EDGE,{"derivedFrom":sQuery(id+"F0.wireOp",EDGE,"E11.1.0.26")}),1.0]])]});
            var Q29;
            Q29=makeQuery(id+"F0.imprint","IMPRINT",FACE,{"disambiguationData":[TD([[makeQuery(id+"F0.imprint","IMPRINT",EDGE,{"derivedFrom":sQuery(id+"F0.wireOp",EDGE,"E11.1.0.24")}),1.0]])]});
            var Q30;
            Q30=makeQuery(id+"F0.imprint","IMPRINT",FACE,{"disambiguationData":[TD([[makeQuery(id+"F0.imprint","IMPRINT",EDGE,{"derivedFrom":sQuery(id+"F0.wireOp",EDGE,"E11.1.0.17")}),1.0]])]});
            var Q31;
            Q31=makeQuery(id+"F0.imprint","IMPRINT",FACE,{"disambiguationData":[TD([[makeQuery(id+"F0.imprint","IMPRINT",EDGE,{"derivedFrom":sQuery(id+"F0.wireOp",EDGE,"E11.1.0.16")}),1.0]])]});
            var Q32;
            Q32=makeQuery(id+"F0.imprint","IMPRINT",FACE,{"disambiguationData":[TD([[makeQuery(id+"F0.imprint","IMPRINT",EDGE,{"derivedFrom":sQuery(id+"F0.wireOp",EDGE,"E11.1.0.15")}),1.0]])]});
            var Q33;
            Q33=makeQuery(id+"F0.imprint","IMPRINT",FACE,{"disambiguationData":[TD([[makeQuery(id+"F0.imprint","IMPRINT",EDGE,{"derivedFrom":sQuery(id+"F0.wireOp",EDGE,"E39.5.0.15")}),1.0]])]});
            var Q34;
            Q34=makeQuery(id+"F0.imprint","IMPRINT",FACE,{"disambiguationData":[TD([[makeQuery(id+"F0.imprint","IMPRINT",EDGE,{"derivedFrom":sQuery(id+"F0.wireOp",EDGE,"E39.4.0.15")}),1.0]])]});
            var Q35;
            Q35=makeQuery(id+"F0.imprint","IMPRINT",FACE,{"disambiguationData":[TD([[makeQuery(id+"F0.imprint","IMPRINT",EDGE,{"derivedFrom":sQuery(id+"F0.wireOp",EDGE,"E39.3.0.15")}),1.0]])]});
            var Q36;
            Q36=makeQuery(id+"F0.imprint","IMPRINT",FACE,{"disambiguationData":[TD([[makeQuery(id+"F0.imprint","IMPRINT",EDGE,{"derivedFrom":sQuery(id+"F0.wireOp",EDGE,"E39.2.0.15")}),1.0]])]});
            var Q37;
            Q37=makeQuery(id+"F0.imprint","IMPRINT",FACE,{"disambiguationData":[TD([[makeQuery(id+"F0.imprint","IMPRINT",EDGE,{"derivedFrom":sQuery(id+"F0.wireOp",EDGE,"E39.1.0.15")}),1.0]])]});
            var Q38;
            Q38=makeQuery(id+"F0.imprint","IMPRINT",FACE,{"disambiguationData":[TD([[makeQuery(id+"F0.imprint","IMPRINT",EDGE,{"derivedFrom":sQuery(id+"F0.wireOp",EDGE,"E23")}),1.0]])]});
            var Q39;
            Q39=makeQuery(id+"F0.imprint","IMPRINT",FACE,{"disambiguationData":[TD([[makeQuery(id+"F0.imprint","IMPRINT",EDGE,{"derivedFrom":sQuery(id+"F0.wireOp",EDGE,"E57")}),1.0]])]});
            var Q40;
            Q40=makeQuery(id+"F0.imprint","IMPRINT",FACE,{"disambiguationData":[TD([[makeQuery(id+"F0.imprint","IMPRINT",EDGE,{"derivedFrom":sQuery(id+"F0.wireOp",EDGE,"E59")}),1.0]])]});
            var Q41;
            Q41=makeQuery(id+"F0.imprint","IMPRINT",FACE,{"disambiguationData":[TD([[makeQuery(id+"F0.imprint","IMPRINT",EDGE,{"derivedFrom":sQuery(id+"F0.wireOp",EDGE,"E60")}),1.0]])]});
            var Q42;
            Q42=makeQuery(id+"F0.imprint","IMPRINT",FACE,{"disambiguationData":[TD([[makeQuery(id+"F0.imprint","IMPRINT",EDGE,{"derivedFrom":sQuery(id+"F0.wireOp",EDGE,"E58")}),1.0]])]});
            var Q43;
            Q43=makeQuery(id+"F0.imprint","IMPRINT",FACE,{"disambiguationData":[TD([[makeQuery(id+"F0.imprint","IMPRINT",EDGE,{"derivedFrom":sQuery(id+"F0.wireOp",EDGE,"E31")}),1.0]])]});
            var Q44;
            Q44=makeQuery(id+"F0.imprint","IMPRINT",FACE,{"disambiguationData":[TD([[makeQuery(id+"F0.imprint","IMPRINT",EDGE,{"derivedFrom":sQuery(id+"F0.wireOp",EDGE,"E29")}),1.0]])]});
            var Q45;
            Q45=makeQuery(id+"F0.imprint","IMPRINT",FACE,{"disambiguationData":[TD([[makeQuery(id+"F0.imprint","IMPRINT",EDGE,{"derivedFrom":sQuery(id+"F0.wireOp",EDGE,"E39.1.0.12")}),1.0]])]});
            var Q46;
            Q46=makeQuery(id+"F0.imprint","IMPRINT",FACE,{"disambiguationData":[TD([[makeQuery(id+"F0.imprint","IMPRINT",EDGE,{"derivedFrom":sQuery(id+"F0.wireOp",EDGE,"E39.1.0.11")}),1.0]])]});
            var Q47;
            Q47=makeQuery(id+"F0.imprint","IMPRINT",FACE,{"disambiguationData":[TD([[makeQuery(id+"F0.imprint","IMPRINT",EDGE,{"derivedFrom":sQuery(id+"F0.wireOp",EDGE,"E39.2.0.11")}),1.0]])]});
            var Q48;
            Q48=makeQuery(id+"F0.imprint","IMPRINT",FACE,{"disambiguationData":[TD([[makeQuery(id+"F0.imprint","IMPRINT",EDGE,{"derivedFrom":sQuery(id+"F0.wireOp",EDGE,"E39.2.0.12")}),1.0]])]});
            var Q49;
            Q49=makeQuery(id+"F0.imprint","IMPRINT",FACE,{"disambiguationData":[TD([[makeQuery(id+"F0.imprint","IMPRINT",EDGE,{"derivedFrom":sQuery(id+"F0.wireOp",EDGE,"E39.3.0.12")}),1.0]])]});
            var Q50;
            Q50=makeQuery(id+"F0.imprint","IMPRINT",FACE,{"disambiguationData":[TD([[makeQuery(id+"F0.imprint","IMPRINT",EDGE,{"derivedFrom":sQuery(id+"F0.wireOp",EDGE,"E39.3.0.11")}),1.0]])]});
            var Q51;
            Q51=makeQuery(id+"F0.imprint","IMPRINT",FACE,{"disambiguationData":[TD([[makeQuery(id+"F0.imprint","IMPRINT",EDGE,{"derivedFrom":sQuery(id+"F0.wireOp",EDGE,"E39.4.0.11")}),1.0]])]});
            var Q52;
            Q52=makeQuery(id+"F0.imprint","IMPRINT",FACE,{"disambiguationData":[TD([[makeQuery(id+"F0.imprint","IMPRINT",EDGE,{"derivedFrom":sQuery(id+"F0.wireOp",EDGE,"E39.4.0.12")}),1.0]])]});
            var Q53;
            Q53=makeQuery(id+"F0.imprint","IMPRINT",FACE,{"disambiguationData":[TD([[makeQuery(id+"F0.imprint","IMPRINT",EDGE,{"derivedFrom":sQuery(id+"F0.wireOp",EDGE,"E39.5.0.12")}),1.0]])]});
            var Q54;
            Q54=makeQuery(id+"F0.imprint","IMPRINT",FACE,{"disambiguationData":[TD([[makeQuery(id+"F0.imprint","IMPRINT",EDGE,{"derivedFrom":sQuery(id+"F0.wireOp",EDGE,"E39.5.0.11")}),1.0]])]});
            var Q55;
            Q55=makeQuery(id+"F0.imprint","IMPRINT",FACE,{"disambiguationData":[TD([[makeQuery(id+"F0.imprint","IMPRINT",EDGE,{"derivedFrom":sQuery(id+"F0.wireOp",EDGE,"E33")}),1.0]])]});
            var Q56;
            Q56=makeQuery(id+"F0.imprint","IMPRINT",FACE,{"disambiguationData":[TD([[makeQuery(id+"F0.imprint","IMPRINT",EDGE,{"derivedFrom":sQuery(id+"F0.wireOp",EDGE,"E39.1.0.2")}),1.0]])]});
            var Q57;
            Q57=makeQuery(id+"F0.imprint","IMPRINT",FACE,{"disambiguationData":[TD([[makeQuery(id+"F0.imprint","IMPRINT",EDGE,{"derivedFrom":sQuery(id+"F0.wireOp",EDGE,"E39.2.0.2")}),1.0]])]});
            var Q58;
            Q58=makeQuery(id+"F0.imprint","IMPRINT",FACE,{"disambiguationData":[TD([[makeQuery(id+"F0.imprint","IMPRINT",EDGE,{"derivedFrom":sQuery(id+"F0.wireOp",EDGE,"E39.3.0.2")}),1.0]])]});
            var Q59;
            Q59=makeQuery(id+"F0.imprint","IMPRINT",FACE,{"disambiguationData":[TD([[makeQuery(id+"F0.imprint","IMPRINT",EDGE,{"derivedFrom":sQuery(id+"F0.wireOp",EDGE,"E39.4.0.2")}),1.0]])]});
            var Q60;
            Q60=makeQuery(id+"F0.imprint","IMPRINT",FACE,{"disambiguationData":[TD([[makeQuery(id+"F0.imprint","IMPRINT",EDGE,{"derivedFrom":sQuery(id+"F0.wireOp",EDGE,"E39.5.0.2")}),1.0]])]});
            var Q61;
            Q61=makeQuery(id+"F0.imprint","IMPRINT",FACE,{"disambiguationData":[TD([[makeQuery(id+"F0.imprint","IMPRINT",EDGE,{"derivedFrom":sQuery(id+"F0.wireOp",EDGE,"E52")}),1.0]])]});
            var Q62;
            Q62=makeQuery(id+"F0.imprint","IMPRINT",FACE,{"disambiguationData":[TD([[makeQuery(id+"F0.imprint","IMPRINT",EDGE,{"derivedFrom":sQuery(id+"F0.wireOp",EDGE,"E15")}),1.0]])]});
            var Q63;
            Q63=makeQuery(id+"F0.imprint","IMPRINT",FACE,{"disambiguationData":[TD([[makeQuery(id+"F0.imprint","IMPRINT",EDGE,{"derivedFrom":sQuery(id+"F0.wireOp",EDGE,"E11.1.0.18")}),1.0]])]});
            var Q64;
            Q64=makeQuery(id+"F0.imprint","IMPRINT",FACE,{"disambiguationData":[TD([[makeQuery(id+"F0.imprint","IMPRINT",EDGE,{"derivedFrom":sQuery(id+"F0.wireOp",EDGE,"E69")}),1.0]])]});
            var Q65;
            Q65=makeQuery(id+"F0.imprint","IMPRINT",FACE,{"disambiguationData":[TD([[makeQuery(id+"F0.imprint","IMPRINT",EDGE,{"derivedFrom":sQuery(id+"F0.wireOp",EDGE,"E70")}),1.0]])]});
            var Q66;
            Q66=makeQuery(id+"F0.imprint","IMPRINT",FACE,{"disambiguationData":[TD([[makeQuery(id+"F0.imprint","IMPRINT",EDGE,{"derivedFrom":sQuery(id+"F0.wireOp",EDGE,"E68")}),1.0]])]});
            extrude(context, id + "F4", {"entities" : qUnion([Q0, Q1, Q2, Q3, Q4, Q5, Q6, Q7, Q8, Q9, Q10, Q11, Q12, Q13, Q14, Q15, Q16, Q17, Q18, Q19, Q20, Q21, Q22, Q23, Q24, Q25, Q26, Q27, Q28, Q29, Q30, Q31, Q32, Q33, Q34, Q35, Q36, Q37, Q38, Q39, Q40, Q41, Q42, Q43, Q44, Q45, Q46, Q47, Q48, Q49, Q50, Q51, Q52, Q53, Q54, Q55, Q56, Q57, Q58, Q59, Q60, Q61, Q62, Q63, Q64, Q65, Q66]), "depth" : .1 * mm, "offsetDistance" : 25 * mm});
        }
        {
            var Q0;
            Q0=makeQuery(id+"F0.imprint","IMPRINT",FACE,{"disambiguationData":[TD([[makeQuery(id+"F0.imprint","IMPRINT",EDGE,{"derivedFrom":sQuery(id+"F0.wireOp",EDGE,"E78.sketch_text.stroke-0")}),-1.0]])]});
            var Q1;
            Q1=makeQuery(id+"F0.imprint","IMPRINT",FACE,{"disambiguationData":[TD([[makeQuery(id+"F0.imprint","IMPRINT",EDGE,{"derivedFrom":sQuery(id+"F0.wireOp",EDGE,"E79.sketch_text.stroke-0")}),-1.0]])]});
            extrude(context, id + "F5", {"entities" : qUnion([Q0, Q1]), "depth" : .1 * mm, "offsetDistance" : 25 * mm});
        }
    });
